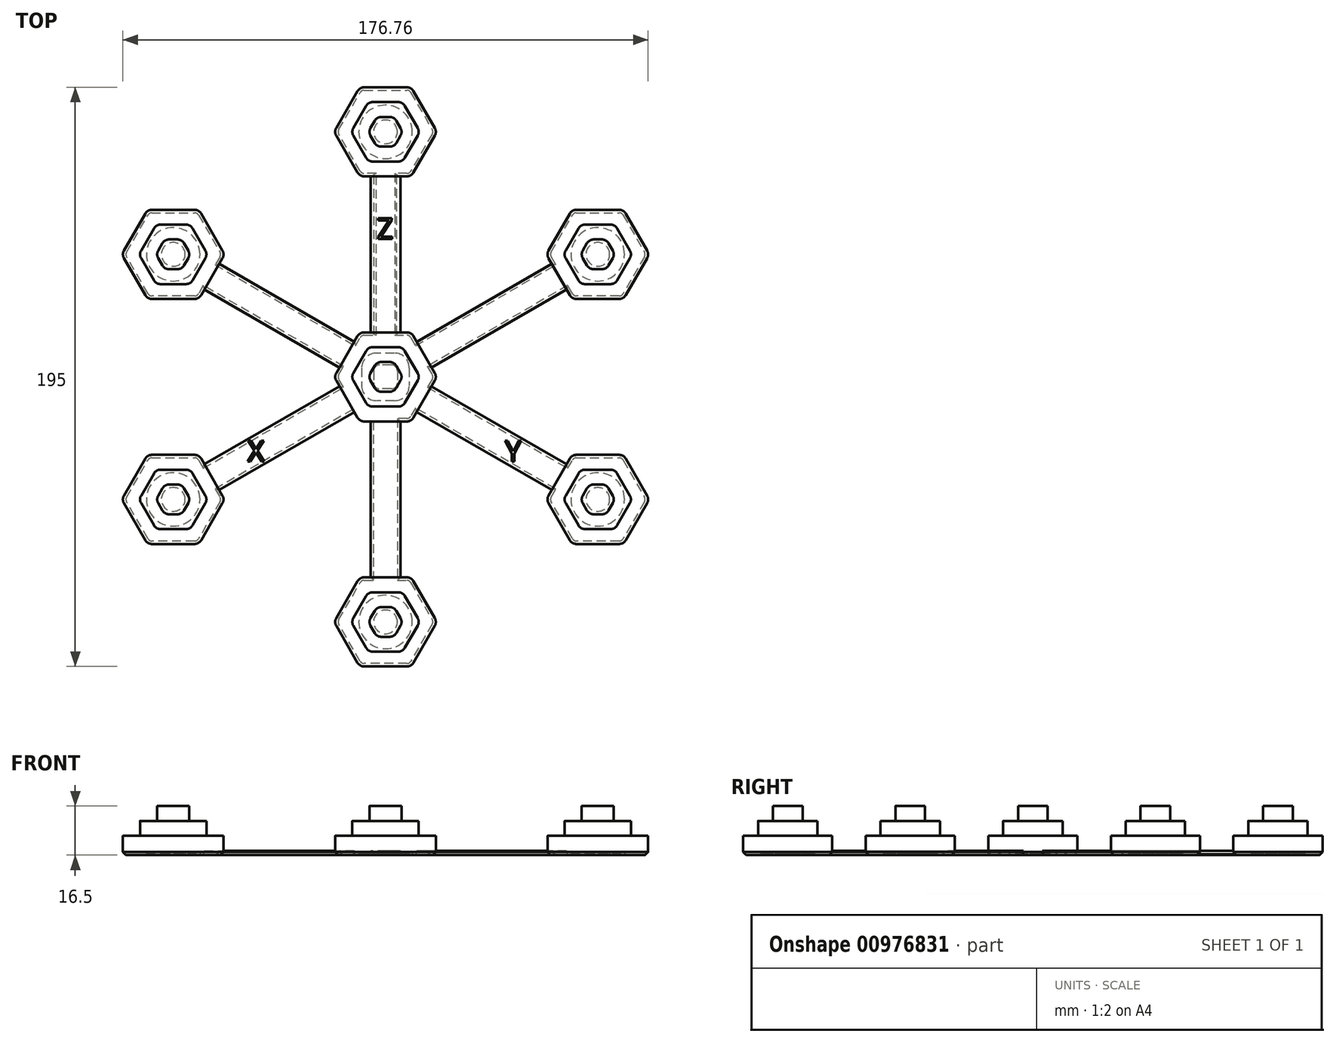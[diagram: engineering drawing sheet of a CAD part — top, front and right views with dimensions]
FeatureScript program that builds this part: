
annotation { "Feature Type Name" : "Feature", "Feature Type Description" : "" }
export const myFeature = defineFeature(function(context is Context, id is Id, definition is map)
    precondition{}
    {
        {
            var Q0;
            Q0=qCreatedBy(makeId("Top.planeOp"),FACE);
            var sketch = newSketch(context, id + "F0", { "sketchPlane" : qUnion([Q0])});
            skCircle(sketch, "E0", {"center": v(0, 0) * mm, "radius": 100 * mm, "construction": true});
            skCircle(sketch, "E1", {"center": v(0, 0) * mm, "radius": 65 * mm, "construction": true});
            skLineSegment(sketch, "E2", {"start": v(0, 0) * mm, "end": v(0, 82.5) * mm, "construction": true});
            skArc(sketch, "E3", {"start": v(5, 68.36) * mm, "mid": v(0, 97.5) * mm, "end": v(-5, 68.36) * mm, "construction": true});
            skLineSegment(sketch, "E4.1.0", {"start": v(0, 0) * mm, "end": v(-71.45, 41.25) * mm, "construction": true});
            skArc(sketch, "E4.1.1", {"start": v(-56.7, 38.5) * mm, "mid": v(-84.44, 48.75) * mm, "end": v(-61.7, 29.85) * mm, "construction": true});
            skLineSegment(sketch, "E4.2.0", {"start": v(0, 0) * mm, "end": v(-71.45, -41.25) * mm, "construction": true});
            skArc(sketch, "E4.2.1", {"start": v(-61.7, -29.85) * mm, "mid": v(-84.44, -48.75) * mm, "end": v(-56.7, -38.5) * mm, "construction": true});
            skLineSegment(sketch, "E4.3.0", {"start": v(0, 0) * mm, "end": v(0, -82.5) * mm, "construction": true});
            skArc(sketch, "E4.3.1", {"start": v(-5, -68.36) * mm, "mid": v(0, -97.5) * mm, "end": v(5, -68.36) * mm, "construction": true});
            skLineSegment(sketch, "E4.4.0", {"start": v(0, 0) * mm, "end": v(71.45, -41.25) * mm, "construction": true});
            skArc(sketch, "E4.4.1", {"start": v(56.7, -38.5) * mm, "mid": v(84.44, -48.75) * mm, "end": v(61.7, -29.85) * mm, "construction": true});
            skLineSegment(sketch, "E4.5.0", {"start": v(0, 0) * mm, "end": v(71.45, 41.25) * mm, "construction": true});
            skArc(sketch, "E4.5.1", {"start": v(61.7, 29.85) * mm, "mid": v(84.44, 48.75) * mm, "end": v(56.7, 38.5) * mm, "construction": true});
            skLineSegment(sketch, "E5.left", {"start": v(-5, 67.5) * mm, "end": v(-5, 15) * mm});
            skLineSegment(sketch, "E5.right", {"start": v(5, 67.5) * mm, "end": v(5, 15) * mm});
            skArc(sketch, "E6.trimOffspring", {"start": v(5, -14.14) * mm, "mid": v(7.5, -13) * mm, "end": v(9.75, -11.4) * mm});
            skCircle(sketch, "E7.cCircle", {"center": v(0, 82.5) * mm, "radius": 15 * mm, "construction": true});
            skLineSegment(sketch, "E7.0", {"start": v(-8.66, 97.5) * mm, "end": v(8.66, 97.5) * mm});
            skLineSegment(sketch, "E7.1", {"start": v(8.66, 97.5) * mm, "end": v(17.32, 82.5) * mm});
            skLineSegment(sketch, "E7.2", {"start": v(17.32, 82.5) * mm, "end": v(8.66, 67.5) * mm});
            skLineSegment(sketch, "E7.3", {"start": v(8.66, 67.5) * mm, "end": v(5, 67.5) * mm});
            skLineSegment(sketch, "E7.4", {"start": v(-8.66, 67.5) * mm, "end": v(-17.32, 82.5) * mm});
            skLineSegment(sketch, "E7.5", {"start": v(-17.32, 82.5) * mm, "end": v(-8.66, 97.5) * mm});
            skPoint(sketch, "E7.0.midPoint", {"position": v(0, 97.5) * mm});
            skLineSegment(sketch, "E8.trimOffspring", {"start": v(-5, 67.5) * mm, "end": v(-8.66, 67.5) * mm});
            skLineSegment(sketch, "E9.1.0", {"start": v(-80.1, 26.25) * mm, "end": v(-88.77, 41.25) * mm});
            skLineSegment(sketch, "E9.1.1", {"start": v(-88.77, 41.25) * mm, "end": v(-80.1, 56.25) * mm});
            skLineSegment(sketch, "E9.1.2", {"start": v(-80.1, 56.25) * mm, "end": v(-62.79, 56.25) * mm});
            skLineSegment(sketch, "E9.1.3", {"start": v(-62.79, 56.25) * mm, "end": v(-54.13, 41.25) * mm});
            skLineSegment(sketch, "E9.1.4", {"start": v(-62.79, 26.25) * mm, "end": v(-80.1, 26.25) * mm});
            skLineSegment(sketch, "E9.1.5", {"start": v(-60.96, 29.42) * mm, "end": v(-62.79, 26.25) * mm});
            skLineSegment(sketch, "E9.1.6", {"start": v(-54.13, 41.25) * mm, "end": v(-55.96, 38.08) * mm});
            skLineSegment(sketch, "E9.1.7", {"start": v(-60.96, 29.42) * mm, "end": v(-15.5, 3.17) * mm});
            skLineSegment(sketch, "E9.1.8", {"start": v(-55.96, 38.08) * mm, "end": v(-10.5, 11.83) * mm});
            skLineSegment(sketch, "E9.2.0", {"start": v(-62.79, -56.25) * mm, "end": v(-80.1, -56.25) * mm});
            skLineSegment(sketch, "E9.2.1", {"start": v(-80.1, -56.25) * mm, "end": v(-88.77, -41.25) * mm});
            skLineSegment(sketch, "E9.2.2", {"start": v(-88.77, -41.25) * mm, "end": v(-80.1, -26.25) * mm});
            skLineSegment(sketch, "E9.2.3", {"start": v(-80.1, -26.25) * mm, "end": v(-62.79, -26.25) * mm});
            skLineSegment(sketch, "E9.2.4", {"start": v(-54.13, -41.25) * mm, "end": v(-62.79, -56.25) * mm});
            skLineSegment(sketch, "E9.2.5", {"start": v(-55.96, -38.08) * mm, "end": v(-54.13, -41.25) * mm});
            skLineSegment(sketch, "E9.2.6", {"start": v(-62.79, -26.25) * mm, "end": v(-60.96, -29.42) * mm});
            skLineSegment(sketch, "E9.2.7", {"start": v(-55.96, -38.08) * mm, "end": v(-10.5, -11.83) * mm});
            skLineSegment(sketch, "E9.2.8", {"start": v(-60.96, -29.42) * mm, "end": v(-15.5, -3.17) * mm});
            skLineSegment(sketch, "E9.3.0", {"start": v(17.32, -82.5) * mm, "end": v(8.66, -97.5) * mm});
            skLineSegment(sketch, "E9.3.1", {"start": v(8.66, -97.5) * mm, "end": v(-8.66, -97.5) * mm});
            skLineSegment(sketch, "E9.3.2", {"start": v(-8.66, -97.5) * mm, "end": v(-17.32, -82.5) * mm});
            skLineSegment(sketch, "E9.3.3", {"start": v(-17.32, -82.5) * mm, "end": v(-8.66, -67.5) * mm});
            skLineSegment(sketch, "E9.3.4", {"start": v(8.66, -67.5) * mm, "end": v(17.32, -82.5) * mm});
            skLineSegment(sketch, "E9.3.5", {"start": v(5, -67.5) * mm, "end": v(8.66, -67.5) * mm});
            skLineSegment(sketch, "E9.3.6", {"start": v(-8.66, -67.5) * mm, "end": v(-5, -67.5) * mm});
            skLineSegment(sketch, "E9.3.7", {"start": v(5, -67.5) * mm, "end": v(5, -15) * mm});
            skLineSegment(sketch, "E9.3.8", {"start": v(-5, -67.5) * mm, "end": v(-5, -15) * mm});
            skLineSegment(sketch, "E9.4.0", {"start": v(80.1, -26.25) * mm, "end": v(88.77, -41.25) * mm});
            skLineSegment(sketch, "E9.4.1", {"start": v(88.77, -41.25) * mm, "end": v(80.1, -56.25) * mm});
            skLineSegment(sketch, "E9.4.2", {"start": v(80.1, -56.25) * mm, "end": v(62.79, -56.25) * mm});
            skLineSegment(sketch, "E9.4.3", {"start": v(62.79, -56.25) * mm, "end": v(54.13, -41.25) * mm});
            skLineSegment(sketch, "E9.4.4", {"start": v(62.79, -26.25) * mm, "end": v(80.1, -26.25) * mm});
            skLineSegment(sketch, "E9.4.5", {"start": v(60.96, -29.42) * mm, "end": v(62.79, -26.25) * mm});
            skLineSegment(sketch, "E9.4.6", {"start": v(54.13, -41.25) * mm, "end": v(55.96, -38.08) * mm});
            skLineSegment(sketch, "E9.4.7", {"start": v(60.96, -29.42) * mm, "end": v(15.5, -3.17) * mm});
            skLineSegment(sketch, "E9.4.8", {"start": v(55.96, -38.08) * mm, "end": v(10.5, -11.83) * mm});
            skLineSegment(sketch, "E9.5.0", {"start": v(62.79, 56.25) * mm, "end": v(80.1, 56.25) * mm});
            skLineSegment(sketch, "E9.5.1", {"start": v(80.1, 56.25) * mm, "end": v(88.77, 41.25) * mm});
            skLineSegment(sketch, "E9.5.2", {"start": v(88.77, 41.25) * mm, "end": v(80.1, 26.25) * mm});
            skLineSegment(sketch, "E9.5.3", {"start": v(80.1, 26.25) * mm, "end": v(62.79, 26.25) * mm});
            skLineSegment(sketch, "E9.5.4", {"start": v(54.13, 41.25) * mm, "end": v(62.79, 56.25) * mm});
            skLineSegment(sketch, "E9.5.5", {"start": v(55.96, 38.08) * mm, "end": v(54.13, 41.25) * mm});
            skLineSegment(sketch, "E9.5.6", {"start": v(62.79, 26.25) * mm, "end": v(60.96, 29.42) * mm});
            skLineSegment(sketch, "E9.5.7", {"start": v(55.96, 38.08) * mm, "end": v(10.5, 11.83) * mm});
            skLineSegment(sketch, "E9.5.8", {"start": v(60.96, 29.42) * mm, "end": v(15.5, 3.17) * mm});
            skCircle(sketch, "E10.cCircle", {"center": v(0, 0) * mm, "radius": 15 * mm, "construction": true});
            skLineSegment(sketch, "E10.0", {"start": v(8.66, -15) * mm, "end": v(5, -15) * mm});
            skLineSegment(sketch, "E10.1", {"start": v(-8.66, -15) * mm, "end": v(-10.5, -11.83) * mm});
            skLineSegment(sketch, "E10.2", {"start": v(-17.32, 0) * mm, "end": v(-15.5, 3.17) * mm});
            skLineSegment(sketch, "E10.3", {"start": v(-8.66, 15) * mm, "end": v(-5, 15) * mm});
            skLineSegment(sketch, "E10.4", {"start": v(8.66, 15) * mm, "end": v(10.5, 11.83) * mm});
            skLineSegment(sketch, "E10.5", {"start": v(17.32, 0) * mm, "end": v(15.5, -3.17) * mm});
            skPoint(sketch, "E10.0.midPoint", {"position": v(0, -15) * mm});
            skLineSegment(sketch, "E11.trimOffspring", {"start": v(5, 15) * mm, "end": v(8.66, 15) * mm});
            skPoint(sketch, "E12.orphan", {"position": v(5, 14.14) * mm});
            skPoint(sketch, "E13.orphan", {"position": v(-5, 14.14) * mm});
            skPoint(sketch, "E14.orphan", {"position": v(-9.75, 11.4) * mm});
            skLineSegment(sketch, "E15.trimOffspring", {"start": v(-10.5, 11.83) * mm, "end": v(-8.66, 15) * mm});
            skPoint(sketch, "E16.orphan", {"position": v(-14.75, 2.74) * mm});
            skLineSegment(sketch, "E17.trimOffspring", {"start": v(-15.5, -3.17) * mm, "end": v(-17.32, 0) * mm});
            skPoint(sketch, "E18.orphan", {"position": v(-14.75, -2.74) * mm});
            skPoint(sketch, "E19.orphan", {"position": v(-9.75, -11.4) * mm});
            skPoint(sketch, "E20.orphan", {"position": v(-5, -14.14) * mm});
            skLineSegment(sketch, "E21.trimOffspring", {"start": v(-5, -15) * mm, "end": v(-8.66, -15) * mm});
            skPoint(sketch, "E22.orphan", {"position": v(5, -14.14) * mm});
            skPoint(sketch, "E23.orphan", {"position": v(9.75, -11.4) * mm});
            skLineSegment(sketch, "E24.trimOffspring", {"start": v(10.5, -11.83) * mm, "end": v(8.66, -15) * mm});
            skPoint(sketch, "E25.orphan", {"position": v(14.75, -2.74) * mm});
            skPoint(sketch, "E26.orphan", {"position": v(9.75, 11.4) * mm});
            skLineSegment(sketch, "E27.trimOffspring", {"start": v(15.5, 3.17) * mm, "end": v(17.32, 0) * mm});
            skPoint(sketch, "E28.orphan", {"position": v(14.75, 2.74) * mm});
            skSolve(sketch);
        }
        {
            var Q0;
            Q0 = qSketchRegion(id + "F0", true);
            extrude(context, id + "F1", {"entities" : qUnion([Q0]), "depth" : 1.5 * mm, "offsetDistance" : 25 * mm});
        }
        {
            var Q0;
            Q0=makeQuery(id+"F1.opExtrude","CAP_FACE",FACE,{"disambiguationData":[OSD([sQuery(id+"F0.wireOp",EDGE,"E3"),sQuery(id+"F0.wireOp",EDGE,"E4.1.1"),sQuery(id+"F0.wireOp",EDGE,"E4.2.1"),sQuery(id+"F0.wireOp",EDGE,"E4.3.1"),sQuery(id+"F0.wireOp",EDGE,"E4.4.1"),sQuery(id+"F0.wireOp",EDGE,"E4.5.1"),sQuery(id+"F0.wireOp",EDGE,"d2wCPqSr-nOOy-JmX4-d6uT-xf62uPJMTqVu"),sQuery(id+"F0.wireOp",EDGE,"E5.left"),sQuery(id+"F0.wireOp",EDGE,"E5.right"),sQuery(id+"F0.wireOp",EDGE,"a48290ef-ed8c-49ca-b5e9-a96a2eef4f7f.1.0"),sQuery(id+"F0.wireOp",EDGE,"a48290ef-ed8c-49ca-b5e9-a96a2eef4f7f.1.2"),sQuery(id+"F0.wireOp",EDGE,"a48290ef-ed8c-49ca-b5e9-a96a2eef4f7f.2.0"),sQuery(id+"F0.wireOp",EDGE,"a48290ef-ed8c-49ca-b5e9-a96a2eef4f7f.2.2"),sQuery(id+"F0.wireOp",EDGE,"a48290ef-ed8c-49ca-b5e9-a96a2eef4f7f.3.0"),sQuery(id+"F0.wireOp",EDGE,"a48290ef-ed8c-49ca-b5e9-a96a2eef4f7f.3.2"),sQuery(id+"F0.wireOp",EDGE,"a48290ef-ed8c-49ca-b5e9-a96a2eef4f7f.4.0"),sQuery(id+"F0.wireOp",EDGE,"a48290ef-ed8c-49ca-b5e9-a96a2eef4f7f.4.2"),sQuery(id+"F0.wireOp",EDGE,"a48290ef-ed8c-49ca-b5e9-a96a2eef4f7f.5.0"),sQuery(id+"F0.wireOp",EDGE,"a48290ef-ed8c-49ca-b5e9-a96a2eef4f7f.5.2"),sQuery(id+"F0.wireOp",EDGE,"11eb75db-823b-41be-87a0-59ebbf35d80a.trimOffspring"),sQuery(id+"F0.wireOp",EDGE,"628562bd-411f-4c63-a98e-b396f9ac0886.trimOffspring"),sQuery(id+"F0.wireOp",EDGE,"E6.trimOffspring"),sQuery(id+"F0.wireOp",EDGE,"74142023-9392-48eb-a980-45bce0a610e0.trimOffspring"),sQuery(id+"F0.wireOp",EDGE,"74d19543-ae01-4b5b-b9fc-349c831204e3.trimOffspring")])],"isStart":false});
            var sketch = newSketch(context, id + "F2", { "sketchPlane" : qUnion([Q0])});
            skCircle(sketch, "E29.cCircle", {"center": v(0, 0) * mm, "radius": 15 * mm, "construction": true});
            skLineSegment(sketch, "E29.0", {"start": v(-8.66, 15) * mm, "end": v(8.66, 15) * mm});
            skLineSegment(sketch, "E29.1", {"start": v(8.66, 15) * mm, "end": v(17.32, 0) * mm});
            skLineSegment(sketch, "E29.2", {"start": v(17.32, 0) * mm, "end": v(8.66, -15) * mm});
            skLineSegment(sketch, "E29.3", {"start": v(8.66, -15) * mm, "end": v(-8.66, -15) * mm});
            skLineSegment(sketch, "E29.4", {"start": v(-8.66, -15) * mm, "end": v(-17.32, 0) * mm});
            skLineSegment(sketch, "E29.5", {"start": v(-17.32, 0) * mm, "end": v(-8.66, 15) * mm});
            skPoint(sketch, "E29.0.midPoint", {"position": v(0, 15) * mm});
            skCircle(sketch, "E30.cCircle", {"center": v(0, 82.5) * mm, "radius": 15 * mm, "construction": true});
            skLineSegment(sketch, "E30.0", {"start": v(-8.66, 97.5) * mm, "end": v(8.66, 97.5) * mm});
            skLineSegment(sketch, "E30.1", {"start": v(8.66, 97.5) * mm, "end": v(17.32, 82.5) * mm});
            skLineSegment(sketch, "E30.2", {"start": v(17.32, 82.5) * mm, "end": v(8.66, 67.5) * mm});
            skLineSegment(sketch, "E30.3", {"start": v(8.66, 67.5) * mm, "end": v(-8.66, 67.5) * mm});
            skLineSegment(sketch, "E30.4", {"start": v(-8.66, 67.5) * mm, "end": v(-17.32, 82.5) * mm});
            skLineSegment(sketch, "E30.5", {"start": v(-17.32, 82.5) * mm, "end": v(-8.66, 97.5) * mm});
            skPoint(sketch, "E30.0.midPoint", {"position": v(0, 97.5) * mm});
            skLineSegment(sketch, "E31.1.0", {"start": v(-80.1, 56.25) * mm, "end": v(-62.79, 56.25) * mm});
            skPoint(sketch, "E31.1.1", {"position": v(-84.44, 48.75) * mm});
            skLineSegment(sketch, "E31.1.2", {"start": v(-62.79, 56.25) * mm, "end": v(-54.13, 41.25) * mm});
            skLineSegment(sketch, "E31.1.3", {"start": v(-80.1, 26.25) * mm, "end": v(-88.77, 41.25) * mm});
            skCircle(sketch, "E31.1.4", {"center": v(-71.45, 41.25) * mm, "radius": 15 * mm, "construction": true});
            skLineSegment(sketch, "E31.1.5", {"start": v(-62.79, 26.25) * mm, "end": v(-80.1, 26.25) * mm});
            skLineSegment(sketch, "E31.1.6", {"start": v(-54.13, 41.25) * mm, "end": v(-62.79, 26.25) * mm});
            skLineSegment(sketch, "E31.1.7", {"start": v(-88.77, 41.25) * mm, "end": v(-80.1, 56.25) * mm});
            skLineSegment(sketch, "E31.2.0", {"start": v(-88.77, -41.25) * mm, "end": v(-80.1, -26.25) * mm});
            skPoint(sketch, "E31.2.1", {"position": v(-84.44, -48.75) * mm});
            skLineSegment(sketch, "E31.2.2", {"start": v(-80.1, -26.25) * mm, "end": v(-62.79, -26.25) * mm});
            skLineSegment(sketch, "E31.2.3", {"start": v(-62.79, -56.25) * mm, "end": v(-80.1, -56.25) * mm});
            skCircle(sketch, "E31.2.4", {"center": v(-71.45, -41.25) * mm, "radius": 15 * mm, "construction": true});
            skLineSegment(sketch, "E31.2.5", {"start": v(-54.13, -41.25) * mm, "end": v(-62.79, -56.25) * mm});
            skLineSegment(sketch, "E31.2.6", {"start": v(-62.79, -26.25) * mm, "end": v(-54.13, -41.25) * mm});
            skLineSegment(sketch, "E31.2.7", {"start": v(-80.1, -56.25) * mm, "end": v(-88.77, -41.25) * mm});
            skLineSegment(sketch, "E31.3.0", {"start": v(-8.66, -97.5) * mm, "end": v(-17.32, -82.5) * mm});
            skPoint(sketch, "E31.3.1", {"position": v(0, -97.5) * mm});
            skLineSegment(sketch, "E31.3.2", {"start": v(-17.32, -82.5) * mm, "end": v(-8.66, -67.5) * mm});
            skLineSegment(sketch, "E31.3.3", {"start": v(17.32, -82.5) * mm, "end": v(8.66, -97.5) * mm});
            skCircle(sketch, "E31.3.4", {"center": v(0, -82.5) * mm, "radius": 15 * mm, "construction": true});
            skLineSegment(sketch, "E31.3.5", {"start": v(8.66, -67.5) * mm, "end": v(17.32, -82.5) * mm});
            skLineSegment(sketch, "E31.3.6", {"start": v(-8.66, -67.5) * mm, "end": v(8.66, -67.5) * mm});
            skLineSegment(sketch, "E31.3.7", {"start": v(8.66, -97.5) * mm, "end": v(-8.66, -97.5) * mm});
            skLineSegment(sketch, "E31.4.0", {"start": v(80.1, -56.25) * mm, "end": v(62.79, -56.25) * mm});
            skPoint(sketch, "E31.4.1", {"position": v(84.44, -48.75) * mm});
            skLineSegment(sketch, "E31.4.2", {"start": v(62.79, -56.25) * mm, "end": v(54.13, -41.25) * mm});
            skLineSegment(sketch, "E31.4.3", {"start": v(80.1, -26.25) * mm, "end": v(88.77, -41.25) * mm});
            skCircle(sketch, "E31.4.4", {"center": v(71.45, -41.25) * mm, "radius": 15 * mm, "construction": true});
            skLineSegment(sketch, "E31.4.5", {"start": v(62.79, -26.25) * mm, "end": v(80.1, -26.25) * mm});
            skLineSegment(sketch, "E31.4.6", {"start": v(54.13, -41.25) * mm, "end": v(62.79, -26.25) * mm});
            skLineSegment(sketch, "E31.4.7", {"start": v(88.77, -41.25) * mm, "end": v(80.1, -56.25) * mm});
            skLineSegment(sketch, "E31.5.0", {"start": v(88.77, 41.25) * mm, "end": v(80.1, 26.25) * mm});
            skPoint(sketch, "E31.5.1", {"position": v(84.44, 48.75) * mm});
            skLineSegment(sketch, "E31.5.2", {"start": v(80.1, 26.25) * mm, "end": v(62.79, 26.25) * mm});
            skLineSegment(sketch, "E31.5.3", {"start": v(62.79, 56.25) * mm, "end": v(80.1, 56.25) * mm});
            skCircle(sketch, "E31.5.4", {"center": v(71.45, 41.25) * mm, "radius": 15 * mm, "construction": true});
            skLineSegment(sketch, "E31.5.5", {"start": v(54.13, 41.25) * mm, "end": v(62.79, 56.25) * mm});
            skLineSegment(sketch, "E31.5.6", {"start": v(62.79, 26.25) * mm, "end": v(54.13, 41.25) * mm});
            skLineSegment(sketch, "E31.5.7", {"start": v(80.1, 56.25) * mm, "end": v(88.77, 41.25) * mm});
            skSolve(sketch);
        }
        {
            var Q0;
            Q0 = qSketchRegion(id + "F2", true);
            extrude(context, id + "F3", {"entities" : qUnion([Q0]), "operationType" : NewBodyOperationType.ADD, "depth" : 5 * mm, "offsetDistance" : 25 * mm});
        }
        {
            var Q0;
            Q0=makeQuery(id+"F1.opExtrude","CAP_EDGE",EDGE,{"disambiguationData":[OSD([sQuery(id+"F0.wireOp",EDGE,"74142023-9392-48eb-a980-45bce0a610e0.trimOffspring")])],"isStart":true});
            var Q1;
            Q1=makeQuery(id+"F1.opExtrude","CAP_EDGE",EDGE,{"disambiguationData":[OSD([sQuery(id+"F0.wireOp",EDGE,"a48290ef-ed8c-49ca-b5e9-a96a2eef4f7f.3.2")])],"isStart":true});
            var Q2;
            Q2=makeQuery(id+"F1.opExtrude","CAP_EDGE",EDGE,{"disambiguationData":[OSD([sQuery(id+"F0.wireOp",EDGE,"E4.3.1")])],"isStart":true});
            var Q3;
            Q3=makeQuery(id+"F1.opExtrude","CAP_EDGE",EDGE,{"disambiguationData":[OSD([sQuery(id+"F0.wireOp",EDGE,"a48290ef-ed8c-49ca-b5e9-a96a2eef4f7f.3.0")])],"isStart":true});
            var Q4;
            Q4=makeQuery(id+"F1.opExtrude","CAP_EDGE",EDGE,{"disambiguationData":[OSD([sQuery(id+"F0.wireOp",EDGE,"E6.trimOffspring")])],"isStart":true});
            var Q5;
            Q5=makeQuery(id+"F1.opExtrude","CAP_EDGE",EDGE,{"disambiguationData":[OSD([sQuery(id+"F0.wireOp",EDGE,"a48290ef-ed8c-49ca-b5e9-a96a2eef4f7f.4.2")])],"isStart":true});
            var Q6;
            Q6=makeQuery(id+"F1.opExtrude","CAP_EDGE",EDGE,{"disambiguationData":[OSD([sQuery(id+"F0.wireOp",EDGE,"E4.4.1")])],"isStart":true});
            var Q7;
            Q7=makeQuery(id+"F1.opExtrude","CAP_EDGE",EDGE,{"disambiguationData":[OSD([sQuery(id+"F0.wireOp",EDGE,"a48290ef-ed8c-49ca-b5e9-a96a2eef4f7f.4.0")])],"isStart":true});
            var Q8;
            Q8=makeQuery(id+"F1.opExtrude","CAP_EDGE",EDGE,{"disambiguationData":[OSD([sQuery(id+"F0.wireOp",EDGE,"628562bd-411f-4c63-a98e-b396f9ac0886.trimOffspring")])],"isStart":true});
            var Q9;
            Q9=makeQuery(id+"F1.opExtrude","CAP_EDGE",EDGE,{"disambiguationData":[OSD([sQuery(id+"F0.wireOp",EDGE,"a48290ef-ed8c-49ca-b5e9-a96a2eef4f7f.5.2")])],"isStart":true});
            var Q10;
            Q10=makeQuery(id+"F1.opExtrude","CAP_EDGE",EDGE,{"disambiguationData":[OSD([sQuery(id+"F0.wireOp",EDGE,"E4.5.1")])],"isStart":true});
            var Q11;
            Q11=makeQuery(id+"F1.opExtrude","CAP_EDGE",EDGE,{"disambiguationData":[OSD([sQuery(id+"F0.wireOp",EDGE,"a48290ef-ed8c-49ca-b5e9-a96a2eef4f7f.5.0")])],"isStart":true});
            var Q12;
            Q12=makeQuery(id+"F1.opExtrude","CAP_EDGE",EDGE,{"disambiguationData":[OSD([sQuery(id+"F0.wireOp",EDGE,"11eb75db-823b-41be-87a0-59ebbf35d80a.trimOffspring")])],"isStart":true});
            var Q13;
            Q13=makeQuery(id+"F1.opExtrude","CAP_EDGE",EDGE,{"disambiguationData":[OSD([sQuery(id+"F0.wireOp",EDGE,"E5.right")])],"isStart":true});
            var Q14;
            Q14=makeQuery(id+"F1.opExtrude","CAP_EDGE",EDGE,{"disambiguationData":[OSD([sQuery(id+"F0.wireOp",EDGE,"E3")])],"isStart":true});
            var Q15;
            Q15=makeQuery(id+"F1.opExtrude","CAP_EDGE",EDGE,{"disambiguationData":[OSD([sQuery(id+"F0.wireOp",EDGE,"E5.left")])],"isStart":true});
            var Q16;
            Q16=makeQuery(id+"F1.opExtrude","CAP_EDGE",EDGE,{"disambiguationData":[OSD([sQuery(id+"F0.wireOp",EDGE,"d2wCPqSr-nOOy-JmX4-d6uT-xf62uPJMTqVu")])],"isStart":true});
            var Q17;
            Q17=makeQuery(id+"F1.opExtrude","CAP_EDGE",EDGE,{"disambiguationData":[OSD([sQuery(id+"F0.wireOp",EDGE,"a48290ef-ed8c-49ca-b5e9-a96a2eef4f7f.1.2")])],"isStart":true});
            var Q18;
            Q18=makeQuery(id+"F1.opExtrude","CAP_EDGE",EDGE,{"disambiguationData":[OSD([sQuery(id+"F0.wireOp",EDGE,"E4.1.1")])],"isStart":true});
            var Q19;
            Q19=makeQuery(id+"F1.opExtrude","CAP_EDGE",EDGE,{"disambiguationData":[OSD([sQuery(id+"F0.wireOp",EDGE,"a48290ef-ed8c-49ca-b5e9-a96a2eef4f7f.1.0")])],"isStart":true});
            var Q20;
            Q20=makeQuery(id+"F1.opExtrude","CAP_EDGE",EDGE,{"disambiguationData":[OSD([sQuery(id+"F0.wireOp",EDGE,"a48290ef-ed8c-49ca-b5e9-a96a2eef4f7f.2.0")])],"isStart":true});
            var Q21;
            Q21=makeQuery(id+"F1.opExtrude","CAP_EDGE",EDGE,{"disambiguationData":[OSD([sQuery(id+"F0.wireOp",EDGE,"74d19543-ae01-4b5b-b9fc-349c831204e3.trimOffspring")])],"isStart":true});
            var Q22;
            Q22=makeQuery(id+"F1.opExtrude","CAP_EDGE",EDGE,{"disambiguationData":[OSD([sQuery(id+"F0.wireOp",EDGE,"a48290ef-ed8c-49ca-b5e9-a96a2eef4f7f.2.2")])],"isStart":true});
            var Q23;
            Q23=makeQuery(id+"F1.opExtrude","CAP_EDGE",EDGE,{"disambiguationData":[OSD([sQuery(id+"F0.wireOp",EDGE,"E4.2.1")])],"isStart":true});
            chamfer(context, id + "F4", {"entities" : qUnion([Q0, Q1, Q2, Q3, Q4, Q5, Q6, Q7, Q8, Q9, Q10, Q11, Q12, Q13, Q14, Q15, Q16, Q17, Q18, Q19, Q20, Q21, Q22, Q23]), "width" : 1.5 * mm, "tangentPropagation" : true});
        }
        {
            var Q0;
            Q0=makeQuery(id+"F3.opExtrude","CAP_FACE",FACE,{"disambiguationData":[OSD([sQuery(id+"F2.wireOp",EDGE,"E29.0"),sQuery(id+"F2.wireOp",EDGE,"E29.1"),sQuery(id+"F2.wireOp",EDGE,"E29.2"),sQuery(id+"F2.wireOp",EDGE,"E29.3"),sQuery(id+"F2.wireOp",EDGE,"E29.4"),sQuery(id+"F2.wireOp",EDGE,"E29.5")])],"isStart":false});
            var sketch = newSketch(context, id + "F5", { "sketchPlane" : qUnion([Q0])});
            skCircle(sketch, "E32.cCircle", {"center": v(0, 0) * mm, "radius": 10 * mm, "construction": true});
            skLineSegment(sketch, "E32.0", {"start": v(-5.77, 10) * mm, "end": v(5.77, 10) * mm});
            skLineSegment(sketch, "E32.1", {"start": v(5.77, 10) * mm, "end": v(11.55, 0) * mm});
            skLineSegment(sketch, "E32.2", {"start": v(11.55, 0) * mm, "end": v(5.77, -10) * mm});
            skLineSegment(sketch, "E32.3", {"start": v(5.77, -10) * mm, "end": v(-5.77, -10) * mm});
            skLineSegment(sketch, "E32.4", {"start": v(-5.77, -10) * mm, "end": v(-11.55, 0) * mm});
            skLineSegment(sketch, "E32.5", {"start": v(-11.55, 0) * mm, "end": v(-5.77, 10) * mm});
            skPoint(sketch, "E32.0.midPoint", {"position": v(0, 10) * mm});
            skCircle(sketch, "E33.cCircle", {"center": v(0, 82.5) * mm, "radius": 10 * mm, "construction": true});
            skLineSegment(sketch, "E33.0", {"start": v(-5.77, 92.5) * mm, "end": v(5.77, 92.5) * mm});
            skLineSegment(sketch, "E33.1", {"start": v(5.77, 92.5) * mm, "end": v(11.55, 82.5) * mm});
            skLineSegment(sketch, "E33.2", {"start": v(11.55, 82.5) * mm, "end": v(5.77, 72.5) * mm});
            skLineSegment(sketch, "E33.3", {"start": v(5.77, 72.5) * mm, "end": v(-5.77, 72.5) * mm});
            skLineSegment(sketch, "E33.4", {"start": v(-5.77, 72.5) * mm, "end": v(-11.55, 82.5) * mm});
            skLineSegment(sketch, "E33.5", {"start": v(-11.55, 82.5) * mm, "end": v(-5.77, 92.5) * mm});
            skPoint(sketch, "E33.0.midPoint", {"position": v(0, 92.5) * mm});
            skLineSegment(sketch, "E34.1.0", {"start": v(-65.67, 51.25) * mm, "end": v(-59.9, 41.25) * mm});
            skLineSegment(sketch, "E34.1.1", {"start": v(-77.22, 51.25) * mm, "end": v(-65.67, 51.25) * mm});
            skLineSegment(sketch, "E34.1.2", {"start": v(-59.9, 41.25) * mm, "end": v(-65.67, 31.25) * mm});
            skCircle(sketch, "E34.1.3", {"center": v(-71.45, 41.25) * mm, "radius": 10 * mm, "construction": true});
            skPoint(sketch, "E34.1.4", {"position": v(-80.1, 46.25) * mm});
            skLineSegment(sketch, "E34.1.5", {"start": v(-65.67, 31.25) * mm, "end": v(-77.22, 31.25) * mm});
            skLineSegment(sketch, "E34.1.6", {"start": v(-77.22, 31.25) * mm, "end": v(-83, 41.25) * mm});
            skLineSegment(sketch, "E34.1.7", {"start": v(-83, 41.25) * mm, "end": v(-77.22, 51.25) * mm});
            skLineSegment(sketch, "E34.2.0", {"start": v(-77.22, -31.25) * mm, "end": v(-65.67, -31.25) * mm});
            skLineSegment(sketch, "E34.2.1", {"start": v(-83, -41.25) * mm, "end": v(-77.22, -31.25) * mm});
            skLineSegment(sketch, "E34.2.2", {"start": v(-65.67, -31.25) * mm, "end": v(-59.9, -41.25) * mm});
            skCircle(sketch, "E34.2.3", {"center": v(-71.45, -41.25) * mm, "radius": 10 * mm, "construction": true});
            skPoint(sketch, "E34.2.4", {"position": v(-80.1, -46.25) * mm});
            skLineSegment(sketch, "E34.2.5", {"start": v(-59.9, -41.25) * mm, "end": v(-65.67, -51.25) * mm});
            skLineSegment(sketch, "E34.2.6", {"start": v(-65.67, -51.25) * mm, "end": v(-77.22, -51.25) * mm});
            skLineSegment(sketch, "E34.2.7", {"start": v(-77.22, -51.25) * mm, "end": v(-83, -41.25) * mm});
            skLineSegment(sketch, "E34.3.0", {"start": v(-11.55, -82.5) * mm, "end": v(-5.77, -72.5) * mm});
            skLineSegment(sketch, "E34.3.1", {"start": v(-5.77, -92.5) * mm, "end": v(-11.55, -82.5) * mm});
            skLineSegment(sketch, "E34.3.2", {"start": v(-5.77, -72.5) * mm, "end": v(5.77, -72.5) * mm});
            skCircle(sketch, "E34.3.3", {"center": v(0, -82.5) * mm, "radius": 10 * mm, "construction": true});
            skPoint(sketch, "E34.3.4", {"position": v(0, -92.5) * mm});
            skLineSegment(sketch, "E34.3.5", {"start": v(5.77, -72.5) * mm, "end": v(11.55, -82.5) * mm});
            skLineSegment(sketch, "E34.3.6", {"start": v(11.55, -82.5) * mm, "end": v(5.77, -92.5) * mm});
            skLineSegment(sketch, "E34.3.7", {"start": v(5.77, -92.5) * mm, "end": v(-5.77, -92.5) * mm});
            skLineSegment(sketch, "E34.4.0", {"start": v(65.67, -51.25) * mm, "end": v(59.9, -41.25) * mm});
            skLineSegment(sketch, "E34.4.1", {"start": v(77.22, -51.25) * mm, "end": v(65.67, -51.25) * mm});
            skLineSegment(sketch, "E34.4.2", {"start": v(59.9, -41.25) * mm, "end": v(65.67, -31.25) * mm});
            skCircle(sketch, "E34.4.3", {"center": v(71.45, -41.25) * mm, "radius": 10 * mm, "construction": true});
            skPoint(sketch, "E34.4.4", {"position": v(80.1, -46.25) * mm});
            skLineSegment(sketch, "E34.4.5", {"start": v(65.67, -31.25) * mm, "end": v(77.22, -31.25) * mm});
            skLineSegment(sketch, "E34.4.6", {"start": v(77.22, -31.25) * mm, "end": v(83, -41.25) * mm});
            skLineSegment(sketch, "E34.4.7", {"start": v(83, -41.25) * mm, "end": v(77.22, -51.25) * mm});
            skLineSegment(sketch, "E34.5.0", {"start": v(77.22, 31.25) * mm, "end": v(65.67, 31.25) * mm});
            skLineSegment(sketch, "E34.5.1", {"start": v(83, 41.25) * mm, "end": v(77.22, 31.25) * mm});
            skLineSegment(sketch, "E34.5.2", {"start": v(65.67, 31.25) * mm, "end": v(59.9, 41.25) * mm});
            skCircle(sketch, "E34.5.3", {"center": v(71.45, 41.25) * mm, "radius": 10 * mm, "construction": true});
            skPoint(sketch, "E34.5.4", {"position": v(80.1, 46.25) * mm});
            skLineSegment(sketch, "E34.5.5", {"start": v(59.9, 41.25) * mm, "end": v(65.67, 51.25) * mm});
            skLineSegment(sketch, "E34.5.6", {"start": v(65.67, 51.25) * mm, "end": v(77.22, 51.25) * mm});
            skLineSegment(sketch, "E34.5.7", {"start": v(77.22, 51.25) * mm, "end": v(83, 41.25) * mm});
            skSolve(sketch);
        }
        {
            var Q0;
            Q0 = qSketchRegion(id + "F5", true);
            extrude(context, id + "F6", {"entities" : qUnion([Q0]), "operationType" : NewBodyOperationType.ADD, "depth" : 5 * mm, "offsetDistance" : 25 * mm});
        }
        {
            var Q0;
            Q0=makeQuery(id+"F6.opExtrude","CAP_FACE",FACE,{"disambiguationData":[OSD([sQuery(id+"F5.wireOp",EDGE,"E32.0"),sQuery(id+"F5.wireOp",EDGE,"E32.1"),sQuery(id+"F5.wireOp",EDGE,"E32.2"),sQuery(id+"F5.wireOp",EDGE,"E32.3"),sQuery(id+"F5.wireOp",EDGE,"E32.4"),sQuery(id+"F5.wireOp",EDGE,"E32.5")])],"isStart":false});
            var sketch = newSketch(context, id + "F7", { "sketchPlane" : qUnion([Q0])});
            skCircle(sketch, "E35.cCircle", {"center": v(0, 0) * mm, "radius": 5 * mm, "construction": true});
            skLineSegment(sketch, "E35.0", {"start": v(-2.89, 5) * mm, "end": v(2.89, 5) * mm});
            skLineSegment(sketch, "E35.1", {"start": v(2.89, 5) * mm, "end": v(5.77, 0) * mm});
            skLineSegment(sketch, "E35.2", {"start": v(5.77, 0) * mm, "end": v(2.89, -5) * mm});
            skLineSegment(sketch, "E35.3", {"start": v(2.89, -5) * mm, "end": v(-2.89, -5) * mm});
            skLineSegment(sketch, "E35.4", {"start": v(-2.89, -5) * mm, "end": v(-5.77, 0) * mm});
            skLineSegment(sketch, "E35.5", {"start": v(-5.77, 0) * mm, "end": v(-2.89, 5) * mm});
            skPoint(sketch, "E35.0.midPoint", {"position": v(0, 5) * mm});
            skCircle(sketch, "E36.cCircle", {"center": v(0, 82.5) * mm, "radius": 5 * mm, "construction": true});
            skLineSegment(sketch, "E36.0", {"start": v(-2.89, 87.5) * mm, "end": v(2.89, 87.5) * mm});
            skLineSegment(sketch, "E36.1", {"start": v(2.89, 87.5) * mm, "end": v(5.77, 82.5) * mm});
            skLineSegment(sketch, "E36.2", {"start": v(5.77, 82.5) * mm, "end": v(2.89, 77.5) * mm});
            skLineSegment(sketch, "E36.3", {"start": v(2.89, 77.5) * mm, "end": v(-2.89, 77.5) * mm});
            skLineSegment(sketch, "E36.4", {"start": v(-2.89, 77.5) * mm, "end": v(-5.77, 82.5) * mm});
            skLineSegment(sketch, "E36.5", {"start": v(-5.77, 82.5) * mm, "end": v(-2.89, 87.5) * mm});
            skPoint(sketch, "E36.0.midPoint", {"position": v(0, 87.5) * mm});
            skPoint(sketch, "E37.1.0", {"position": v(-75.78, 43.75) * mm});
            skLineSegment(sketch, "E37.1.1", {"start": v(-74.33, 46.25) * mm, "end": v(-68.56, 46.25) * mm});
            skLineSegment(sketch, "E37.1.2", {"start": v(-68.56, 46.25) * mm, "end": v(-65.67, 41.25) * mm});
            skLineSegment(sketch, "E37.1.3", {"start": v(-65.67, 41.25) * mm, "end": v(-68.56, 36.25) * mm});
            skLineSegment(sketch, "E37.1.4", {"start": v(-74.33, 36.25) * mm, "end": v(-77.22, 41.25) * mm});
            skLineSegment(sketch, "E37.1.5", {"start": v(-77.22, 41.25) * mm, "end": v(-74.33, 46.25) * mm});
            skLineSegment(sketch, "E37.1.6", {"start": v(-68.56, 36.25) * mm, "end": v(-74.33, 36.25) * mm});
            skCircle(sketch, "E37.1.7", {"center": v(-71.45, 41.25) * mm, "radius": 5 * mm, "construction": true});
            skPoint(sketch, "E37.2.0", {"position": v(-75.78, -43.75) * mm});
            skLineSegment(sketch, "E37.2.1", {"start": v(-77.22, -41.25) * mm, "end": v(-74.33, -36.25) * mm});
            skLineSegment(sketch, "E37.2.2", {"start": v(-74.33, -36.25) * mm, "end": v(-68.56, -36.25) * mm});
            skLineSegment(sketch, "E37.2.3", {"start": v(-68.56, -36.25) * mm, "end": v(-65.67, -41.25) * mm});
            skLineSegment(sketch, "E37.2.4", {"start": v(-68.56, -46.25) * mm, "end": v(-74.33, -46.25) * mm});
            skLineSegment(sketch, "E37.2.5", {"start": v(-74.33, -46.25) * mm, "end": v(-77.22, -41.25) * mm});
            skLineSegment(sketch, "E37.2.6", {"start": v(-65.67, -41.25) * mm, "end": v(-68.56, -46.25) * mm});
            skCircle(sketch, "E37.2.7", {"center": v(-71.45, -41.25) * mm, "radius": 5 * mm, "construction": true});
            skPoint(sketch, "E37.3.0", {"position": v(0, -87.5) * mm});
            skLineSegment(sketch, "E37.3.1", {"start": v(-2.89, -87.5) * mm, "end": v(-5.77, -82.5) * mm});
            skLineSegment(sketch, "E37.3.2", {"start": v(-5.77, -82.5) * mm, "end": v(-2.89, -77.5) * mm});
            skLineSegment(sketch, "E37.3.3", {"start": v(-2.89, -77.5) * mm, "end": v(2.89, -77.5) * mm});
            skLineSegment(sketch, "E37.3.4", {"start": v(5.77, -82.5) * mm, "end": v(2.89, -87.5) * mm});
            skLineSegment(sketch, "E37.3.5", {"start": v(2.89, -87.5) * mm, "end": v(-2.89, -87.5) * mm});
            skLineSegment(sketch, "E37.3.6", {"start": v(2.89, -77.5) * mm, "end": v(5.77, -82.5) * mm});
            skCircle(sketch, "E37.3.7", {"center": v(0, -82.5) * mm, "radius": 5 * mm, "construction": true});
            skPoint(sketch, "E37.4.0", {"position": v(75.78, -43.75) * mm});
            skLineSegment(sketch, "E37.4.1", {"start": v(74.33, -46.25) * mm, "end": v(68.56, -46.25) * mm});
            skLineSegment(sketch, "E37.4.2", {"start": v(68.56, -46.25) * mm, "end": v(65.67, -41.25) * mm});
            skLineSegment(sketch, "E37.4.3", {"start": v(65.67, -41.25) * mm, "end": v(68.56, -36.25) * mm});
            skLineSegment(sketch, "E37.4.4", {"start": v(74.33, -36.25) * mm, "end": v(77.22, -41.25) * mm});
            skLineSegment(sketch, "E37.4.5", {"start": v(77.22, -41.25) * mm, "end": v(74.33, -46.25) * mm});
            skLineSegment(sketch, "E37.4.6", {"start": v(68.56, -36.25) * mm, "end": v(74.33, -36.25) * mm});
            skCircle(sketch, "E37.4.7", {"center": v(71.45, -41.25) * mm, "radius": 5 * mm, "construction": true});
            skPoint(sketch, "E37.5.0", {"position": v(75.78, 43.75) * mm});
            skLineSegment(sketch, "E37.5.1", {"start": v(77.22, 41.25) * mm, "end": v(74.33, 36.25) * mm});
            skLineSegment(sketch, "E37.5.2", {"start": v(74.33, 36.25) * mm, "end": v(68.56, 36.25) * mm});
            skLineSegment(sketch, "E37.5.3", {"start": v(68.56, 36.25) * mm, "end": v(65.67, 41.25) * mm});
            skLineSegment(sketch, "E37.5.4", {"start": v(68.56, 46.25) * mm, "end": v(74.33, 46.25) * mm});
            skLineSegment(sketch, "E37.5.5", {"start": v(74.33, 46.25) * mm, "end": v(77.22, 41.25) * mm});
            skLineSegment(sketch, "E37.5.6", {"start": v(65.67, 41.25) * mm, "end": v(68.56, 46.25) * mm});
            skCircle(sketch, "E37.5.7", {"center": v(71.45, 41.25) * mm, "radius": 5 * mm, "construction": true});
            skSolve(sketch);
        }
        {
            var Q0;
            Q0 = qSketchRegion(id + "F7", true);
            extrude(context, id + "F8", {"entities" : qUnion([Q0]), "operationType" : NewBodyOperationType.ADD, "depth" : 5 * mm, "offsetDistance" : 25 * mm});
        }
        {
            var Q0;
            Q0=makeQuery(id+"F1.opExtrude","CAP_FACE",FACE,{"disambiguationData":[OSD([sQuery(id+"F0.wireOp",EDGE,"E3"),sQuery(id+"F0.wireOp",EDGE,"E4.1.1"),sQuery(id+"F0.wireOp",EDGE,"E4.2.1"),sQuery(id+"F0.wireOp",EDGE,"E4.3.1"),sQuery(id+"F0.wireOp",EDGE,"E4.4.1"),sQuery(id+"F0.wireOp",EDGE,"E4.5.1"),sQuery(id+"F0.wireOp",EDGE,"d2wCPqSr-nOOy-JmX4-d6uT-xf62uPJMTqVu"),sQuery(id+"F0.wireOp",EDGE,"E5.left"),sQuery(id+"F0.wireOp",EDGE,"E5.right"),sQuery(id+"F0.wireOp",EDGE,"a48290ef-ed8c-49ca-b5e9-a96a2eef4f7f.1.0"),sQuery(id+"F0.wireOp",EDGE,"a48290ef-ed8c-49ca-b5e9-a96a2eef4f7f.1.2"),sQuery(id+"F0.wireOp",EDGE,"a48290ef-ed8c-49ca-b5e9-a96a2eef4f7f.2.0"),sQuery(id+"F0.wireOp",EDGE,"a48290ef-ed8c-49ca-b5e9-a96a2eef4f7f.2.2"),sQuery(id+"F0.wireOp",EDGE,"a48290ef-ed8c-49ca-b5e9-a96a2eef4f7f.3.0"),sQuery(id+"F0.wireOp",EDGE,"a48290ef-ed8c-49ca-b5e9-a96a2eef4f7f.3.2"),sQuery(id+"F0.wireOp",EDGE,"a48290ef-ed8c-49ca-b5e9-a96a2eef4f7f.4.0"),sQuery(id+"F0.wireOp",EDGE,"a48290ef-ed8c-49ca-b5e9-a96a2eef4f7f.4.2"),sQuery(id+"F0.wireOp",EDGE,"a48290ef-ed8c-49ca-b5e9-a96a2eef4f7f.5.0"),sQuery(id+"F0.wireOp",EDGE,"a48290ef-ed8c-49ca-b5e9-a96a2eef4f7f.5.2"),sQuery(id+"F0.wireOp",EDGE,"11eb75db-823b-41be-87a0-59ebbf35d80a.trimOffspring"),sQuery(id+"F0.wireOp",EDGE,"628562bd-411f-4c63-a98e-b396f9ac0886.trimOffspring"),sQuery(id+"F0.wireOp",EDGE,"E6.trimOffspring"),sQuery(id+"F0.wireOp",EDGE,"74142023-9392-48eb-a980-45bce0a610e0.trimOffspring"),sQuery(id+"F0.wireOp",EDGE,"74d19543-ae01-4b5b-b9fc-349c831204e3.trimOffspring")])],"isStart":true});
            var sketch = newSketch(context, id + "F9", { "sketchPlane" : qUnion([Q0])});
            skLineSegment(sketch, "E38.bottom", {"start": v(8, -8) * mm, "end": v(-8, -8) * mm});
            skLineSegment(sketch, "E38.top", {"start": v(8, 8) * mm, "end": v(-8, 8) * mm});
            skLineSegment(sketch, "E38.left", {"start": v(8, -8) * mm, "end": v(8, 8) * mm});
            skLineSegment(sketch, "E38.right", {"start": v(-8, -8) * mm, "end": v(-8, 8) * mm});
            skPoint(sketch, "E38.middle", {"position": v(0, 0) * mm});
            skLineSegment(sketch, "E39.bottom", {"start": v(4, -4) * mm, "end": v(-4, -4) * mm});
            skLineSegment(sketch, "E39.top", {"start": v(4, 4) * mm, "end": v(-4, 4) * mm});
            skLineSegment(sketch, "E39.left", {"start": v(4, -4) * mm, "end": v(4, 4) * mm});
            skLineSegment(sketch, "E39.right", {"start": v(-4, -4) * mm, "end": v(-4, 4) * mm});
            skSolve(sketch);
        }
        {
            var Q0;
            Q0 = qSketchRegion(id + "F9", true);
            extrude(context, id + "F10", {"entities" : qUnion([Q0]), "operationType" : NewBodyOperationType.REMOVE, "oppositeDirection" : true, "depth" : 0.5 * mm, "offsetDistance" : 25 * mm});
        }
        {
            var Q0;
            Q0=makeQuery(id+"F10.boolean.opBoolean","COPY",EDGE,{"derivedFrom":makeQuery(id+"F10.opExtrude","SWEPT_EDGE",EDGE,{"disambiguationData":[OSD([sQuery(id+"F9.wireOp",EDGE,"E38.top"),sQuery(id+"F9.wireOp",EDGE,"E38.right")])]})});
            var Q1;
            Q1=makeQuery(id+"F10.boolean.opBoolean","COPY",EDGE,{"derivedFrom":makeQuery(id+"F10.opExtrude","SWEPT_EDGE",EDGE,{"disambiguationData":[OSD([sQuery(id+"F9.wireOp",EDGE,"E38.top"),sQuery(id+"F9.wireOp",EDGE,"E38.left")])]})});
            var Q2;
            Q2=makeQuery(id+"F10.boolean.opBoolean","COPY",EDGE,{"derivedFrom":makeQuery(id+"F10.opExtrude","SWEPT_EDGE",EDGE,{"disambiguationData":[OSD([sQuery(id+"F9.wireOp",EDGE,"E38.bottom"),sQuery(id+"F9.wireOp",EDGE,"E38.left")])]})});
            var Q3;
            Q3=makeQuery(id+"F10.boolean.opBoolean","COPY",EDGE,{"derivedFrom":makeQuery(id+"F10.opExtrude","SWEPT_EDGE",EDGE,{"disambiguationData":[OSD([sQuery(id+"F9.wireOp",EDGE,"E38.bottom"),sQuery(id+"F9.wireOp",EDGE,"E38.right")])]})});
            fillet(context, id + "F11", {"entities" : qUnion([Q0, Q1, Q2, Q3]), "radius" : 5 * mm, "tangentPropagation" : true, "allowEdgeOverflow" : false});
        }
        {
            var Q0;
            Q0=makeQuery(id+"F10.boolean.opBoolean","COPY",EDGE,{"derivedFrom":makeQuery(id+"F10.opExtrude","SWEPT_EDGE",EDGE,{"disambiguationData":[OSD([sQuery(id+"F9.wireOp",EDGE,"E39.bottom"),sQuery(id+"F9.wireOp",EDGE,"E39.left")])]})});
            var Q1;
            Q1=makeQuery(id+"F10.boolean.opBoolean","COPY",EDGE,{"derivedFrom":makeQuery(id+"F10.opExtrude","SWEPT_EDGE",EDGE,{"disambiguationData":[OSD([sQuery(id+"F9.wireOp",EDGE,"E39.bottom"),sQuery(id+"F9.wireOp",EDGE,"E39.right")])]})});
            var Q2;
            Q2=makeQuery(id+"F10.boolean.opBoolean","COPY",EDGE,{"derivedFrom":makeQuery(id+"F10.opExtrude","SWEPT_EDGE",EDGE,{"disambiguationData":[OSD([sQuery(id+"F9.wireOp",EDGE,"E39.top"),sQuery(id+"F9.wireOp",EDGE,"E39.right")])]})});
            var Q3;
            Q3=makeQuery(id+"F10.boolean.opBoolean","COPY",EDGE,{"derivedFrom":makeQuery(id+"F10.opExtrude","SWEPT_EDGE",EDGE,{"disambiguationData":[OSD([sQuery(id+"F9.wireOp",EDGE,"E39.top"),sQuery(id+"F9.wireOp",EDGE,"E39.left")])]})});
            fillet(context, id + "F12", {"entities" : qUnion([Q0, Q1, Q2, Q3]), "radius" : 2 * mm, "tangentPropagation" : true, "allowEdgeOverflow" : false});
        }
        {
            var Q0;
            Q0=makeQuery(id+"F3.boolean.opBoolean","MERGE",EDGE,{"derivedFrom":[makeQuery(id+"F1.opExtrude","SWEPT_EDGE",EDGE,{"disambiguationData":[OSD([sQuery(id+"F0.wireOp",EDGE,"E9.3.1"),sQuery(id+"F0.wireOp",EDGE,"E9.3.2")])]}),makeQuery(id+"F3.opExtrude","SWEPT_EDGE",EDGE,{"disambiguationData":[OSD([sQuery(id+"F2.wireOp",EDGE,"E31.3.0"),sQuery(id+"F2.wireOp",EDGE,"E31.3.7")])]})]});
            var Q1;
            Q1=makeQuery(id+"F3.boolean.opBoolean","MERGE",EDGE,{"derivedFrom":[makeQuery(id+"F1.opExtrude","SWEPT_EDGE",EDGE,{"disambiguationData":[OSD([sQuery(id+"F0.wireOp",EDGE,"E9.3.0"),sQuery(id+"F0.wireOp",EDGE,"E9.3.1")])]}),makeQuery(id+"F3.opExtrude","SWEPT_EDGE",EDGE,{"disambiguationData":[OSD([sQuery(id+"F2.wireOp",EDGE,"E31.3.3"),sQuery(id+"F2.wireOp",EDGE,"E31.3.7")])]})]});
            var Q2;
            Q2=makeQuery(id+"F3.boolean.opBoolean","MERGE",EDGE,{"derivedFrom":[makeQuery(id+"F1.opExtrude","SWEPT_EDGE",EDGE,{"disambiguationData":[OSD([sQuery(id+"F0.wireOp",EDGE,"E9.3.0"),sQuery(id+"F0.wireOp",EDGE,"E9.3.4")])]}),makeQuery(id+"F3.opExtrude","SWEPT_EDGE",EDGE,{"disambiguationData":[OSD([sQuery(id+"F2.wireOp",EDGE,"E31.3.3"),sQuery(id+"F2.wireOp",EDGE,"E31.3.5")])]})]});
            var Q3;
            Q3=makeQuery(id+"F3.boolean.opBoolean","MERGE",EDGE,{"derivedFrom":[makeQuery(id+"F1.opExtrude","SWEPT_EDGE",EDGE,{"disambiguationData":[OSD([sQuery(id+"F0.wireOp",EDGE,"E9.3.4"),sQuery(id+"F0.wireOp",EDGE,"E9.3.5")])]}),makeQuery(id+"F3.opExtrude","SWEPT_EDGE",EDGE,{"disambiguationData":[OSD([sQuery(id+"F2.wireOp",EDGE,"E31.3.5"),sQuery(id+"F2.wireOp",EDGE,"E31.3.6")])]})]});
            var Q4;
            Q4=makeQuery(id+"F3.boolean.opBoolean","MERGE",EDGE,{"derivedFrom":[makeQuery(id+"F1.opExtrude","SWEPT_EDGE",EDGE,{"disambiguationData":[OSD([sQuery(id+"F0.wireOp",EDGE,"E9.3.3"),sQuery(id+"F0.wireOp",EDGE,"E9.3.6")])]}),makeQuery(id+"F3.opExtrude","SWEPT_EDGE",EDGE,{"disambiguationData":[OSD([sQuery(id+"F2.wireOp",EDGE,"E31.3.2"),sQuery(id+"F2.wireOp",EDGE,"E31.3.6")])]})]});
            var Q5;
            Q5=makeQuery(id+"F3.boolean.opBoolean","MERGE",EDGE,{"derivedFrom":[makeQuery(id+"F1.opExtrude","SWEPT_EDGE",EDGE,{"disambiguationData":[OSD([sQuery(id+"F0.wireOp",EDGE,"E9.3.2"),sQuery(id+"F0.wireOp",EDGE,"E9.3.3")])]}),makeQuery(id+"F3.opExtrude","SWEPT_EDGE",EDGE,{"disambiguationData":[OSD([sQuery(id+"F2.wireOp",EDGE,"E31.3.0"),sQuery(id+"F2.wireOp",EDGE,"E31.3.2")])]})]});
            var Q6;
            Q6=makeQuery(id+"F6.opExtrude","SWEPT_EDGE",EDGE,{"disambiguationData":[OSD([sQuery(id+"F5.wireOp",EDGE,"E34.3.1"),sQuery(id+"F5.wireOp",EDGE,"E34.3.7")])]});
            var Q7;
            Q7=makeQuery(id+"F6.opExtrude","SWEPT_EDGE",EDGE,{"disambiguationData":[OSD([sQuery(id+"F5.wireOp",EDGE,"E34.3.0"),sQuery(id+"F5.wireOp",EDGE,"E34.3.1")])]});
            var Q8;
            Q8=makeQuery(id+"F6.opExtrude","SWEPT_EDGE",EDGE,{"disambiguationData":[OSD([sQuery(id+"F5.wireOp",EDGE,"E34.3.0"),sQuery(id+"F5.wireOp",EDGE,"E34.3.2")])]});
            var Q9;
            Q9=makeQuery(id+"F6.opExtrude","SWEPT_EDGE",EDGE,{"disambiguationData":[OSD([sQuery(id+"F5.wireOp",EDGE,"E34.3.2"),sQuery(id+"F5.wireOp",EDGE,"E34.3.5")])]});
            var Q10;
            Q10=makeQuery(id+"F6.opExtrude","SWEPT_EDGE",EDGE,{"disambiguationData":[OSD([sQuery(id+"F5.wireOp",EDGE,"E34.3.5"),sQuery(id+"F5.wireOp",EDGE,"E34.3.6")])]});
            var Q11;
            Q11=makeQuery(id+"F6.opExtrude","SWEPT_EDGE",EDGE,{"disambiguationData":[OSD([sQuery(id+"F5.wireOp",EDGE,"E34.3.6"),sQuery(id+"F5.wireOp",EDGE,"E34.3.7")])]});
            var Q12;
            Q12=makeQuery(id+"F8.opExtrude","SWEPT_EDGE",EDGE,{"disambiguationData":[OSD([sQuery(id+"F7.wireOp",EDGE,"E37.3.4"),sQuery(id+"F7.wireOp",EDGE,"E37.3.5")])]});
            var Q13;
            Q13=makeQuery(id+"F8.opExtrude","SWEPT_EDGE",EDGE,{"disambiguationData":[OSD([sQuery(id+"F7.wireOp",EDGE,"E37.3.1"),sQuery(id+"F7.wireOp",EDGE,"E37.3.5")])]});
            var Q14;
            Q14=makeQuery(id+"F8.opExtrude","SWEPT_EDGE",EDGE,{"disambiguationData":[OSD([sQuery(id+"F7.wireOp",EDGE,"E37.3.1"),sQuery(id+"F7.wireOp",EDGE,"E37.3.2")])]});
            var Q15;
            Q15=makeQuery(id+"F8.opExtrude","SWEPT_EDGE",EDGE,{"disambiguationData":[OSD([sQuery(id+"F7.wireOp",EDGE,"E37.3.2"),sQuery(id+"F7.wireOp",EDGE,"E37.3.3")])]});
            var Q16;
            Q16=makeQuery(id+"F8.opExtrude","SWEPT_EDGE",EDGE,{"disambiguationData":[OSD([sQuery(id+"F7.wireOp",EDGE,"E37.3.4"),sQuery(id+"F7.wireOp",EDGE,"E37.3.6")])]});
            var Q17;
            Q17=makeQuery(id+"F8.opExtrude","SWEPT_EDGE",EDGE,{"disambiguationData":[OSD([sQuery(id+"F7.wireOp",EDGE,"E37.3.3"),sQuery(id+"F7.wireOp",EDGE,"E37.3.6")])]});
            var Q18;
            Q18=makeQuery(id+"F3.boolean.opBoolean","MERGE",EDGE,{"derivedFrom":[makeQuery(id+"F1.opExtrude","SWEPT_EDGE",EDGE,{"disambiguationData":[OSD([sQuery(id+"F0.wireOp",EDGE,"E9.2.0"),sQuery(id+"F0.wireOp",EDGE,"E9.2.4")])]}),makeQuery(id+"F3.opExtrude","SWEPT_EDGE",EDGE,{"disambiguationData":[OSD([sQuery(id+"F2.wireOp",EDGE,"E31.2.3"),sQuery(id+"F2.wireOp",EDGE,"E31.2.5")])]})]});
            var Q19;
            Q19=makeQuery(id+"F3.boolean.opBoolean","MERGE",EDGE,{"derivedFrom":[makeQuery(id+"F1.opExtrude","SWEPT_EDGE",EDGE,{"disambiguationData":[OSD([sQuery(id+"F0.wireOp",EDGE,"E9.2.0"),sQuery(id+"F0.wireOp",EDGE,"E9.2.1")])]}),makeQuery(id+"F3.opExtrude","SWEPT_EDGE",EDGE,{"disambiguationData":[OSD([sQuery(id+"F2.wireOp",EDGE,"E31.2.3"),sQuery(id+"F2.wireOp",EDGE,"E31.2.7")])]})]});
            var Q20;
            Q20=makeQuery(id+"F3.boolean.opBoolean","MERGE",EDGE,{"derivedFrom":[makeQuery(id+"F1.opExtrude","SWEPT_EDGE",EDGE,{"disambiguationData":[OSD([sQuery(id+"F0.wireOp",EDGE,"E9.2.1"),sQuery(id+"F0.wireOp",EDGE,"E9.2.2")])]}),makeQuery(id+"F3.opExtrude","SWEPT_EDGE",EDGE,{"disambiguationData":[OSD([sQuery(id+"F2.wireOp",EDGE,"E31.2.0"),sQuery(id+"F2.wireOp",EDGE,"E31.2.7")])]})]});
            var Q21;
            Q21=makeQuery(id+"F3.boolean.opBoolean","MERGE",EDGE,{"derivedFrom":[makeQuery(id+"F1.opExtrude","SWEPT_EDGE",EDGE,{"disambiguationData":[OSD([sQuery(id+"F0.wireOp",EDGE,"E9.2.2"),sQuery(id+"F0.wireOp",EDGE,"E9.2.3")])]}),makeQuery(id+"F3.opExtrude","SWEPT_EDGE",EDGE,{"disambiguationData":[OSD([sQuery(id+"F2.wireOp",EDGE,"E31.2.0"),sQuery(id+"F2.wireOp",EDGE,"E31.2.2")])]})]});
            var Q22;
            Q22=makeQuery(id+"F3.boolean.opBoolean","MERGE",EDGE,{"derivedFrom":[makeQuery(id+"F1.opExtrude","SWEPT_EDGE",EDGE,{"disambiguationData":[OSD([sQuery(id+"F0.wireOp",EDGE,"E9.2.4"),sQuery(id+"F0.wireOp",EDGE,"E9.2.5")])]}),makeQuery(id+"F3.opExtrude","SWEPT_EDGE",EDGE,{"disambiguationData":[OSD([sQuery(id+"F2.wireOp",EDGE,"E31.2.5"),sQuery(id+"F2.wireOp",EDGE,"E31.2.6")])]})]});
            var Q23;
            Q23=makeQuery(id+"F3.boolean.opBoolean","MERGE",EDGE,{"derivedFrom":[makeQuery(id+"F1.opExtrude","SWEPT_EDGE",EDGE,{"disambiguationData":[OSD([sQuery(id+"F0.wireOp",EDGE,"E9.2.3"),sQuery(id+"F0.wireOp",EDGE,"E9.2.6")])]}),makeQuery(id+"F3.opExtrude","SWEPT_EDGE",EDGE,{"disambiguationData":[OSD([sQuery(id+"F2.wireOp",EDGE,"E31.2.2"),sQuery(id+"F2.wireOp",EDGE,"E31.2.6")])]})]});
            var Q24;
            Q24=makeQuery(id+"F6.opExtrude","SWEPT_EDGE",EDGE,{"disambiguationData":[OSD([sQuery(id+"F5.wireOp",EDGE,"E34.2.2"),sQuery(id+"F5.wireOp",EDGE,"E34.2.5")])]});
            var Q25;
            Q25=makeQuery(id+"F6.opExtrude","SWEPT_EDGE",EDGE,{"disambiguationData":[OSD([sQuery(id+"F5.wireOp",EDGE,"E34.2.0"),sQuery(id+"F5.wireOp",EDGE,"E34.2.2")])]});
            var Q26;
            Q26=makeQuery(id+"F6.opExtrude","SWEPT_EDGE",EDGE,{"disambiguationData":[OSD([sQuery(id+"F5.wireOp",EDGE,"E34.2.5"),sQuery(id+"F5.wireOp",EDGE,"E34.2.6")])]});
            var Q27;
            Q27=makeQuery(id+"F6.opExtrude","SWEPT_EDGE",EDGE,{"disambiguationData":[OSD([sQuery(id+"F5.wireOp",EDGE,"E34.2.6"),sQuery(id+"F5.wireOp",EDGE,"E34.2.7")])]});
            var Q28;
            Q28=makeQuery(id+"F6.opExtrude","SWEPT_EDGE",EDGE,{"disambiguationData":[OSD([sQuery(id+"F5.wireOp",EDGE,"E34.2.1"),sQuery(id+"F5.wireOp",EDGE,"E34.2.7")])]});
            var Q29;
            Q29=makeQuery(id+"F6.opExtrude","SWEPT_EDGE",EDGE,{"disambiguationData":[OSD([sQuery(id+"F5.wireOp",EDGE,"E34.2.0"),sQuery(id+"F5.wireOp",EDGE,"E34.2.1")])]});
            var Q30;
            Q30=makeQuery(id+"F8.opExtrude","SWEPT_EDGE",EDGE,{"disambiguationData":[OSD([sQuery(id+"F7.wireOp",EDGE,"E37.2.1"),sQuery(id+"F7.wireOp",EDGE,"E37.2.5")])]});
            var Q31;
            Q31=makeQuery(id+"F8.opExtrude","SWEPT_EDGE",EDGE,{"disambiguationData":[OSD([sQuery(id+"F7.wireOp",EDGE,"E37.2.4"),sQuery(id+"F7.wireOp",EDGE,"E37.2.5")])]});
            var Q32;
            Q32=makeQuery(id+"F8.opExtrude","SWEPT_EDGE",EDGE,{"disambiguationData":[OSD([sQuery(id+"F7.wireOp",EDGE,"E37.2.4"),sQuery(id+"F7.wireOp",EDGE,"E37.2.6")])]});
            var Q33;
            Q33=makeQuery(id+"F8.opExtrude","SWEPT_EDGE",EDGE,{"disambiguationData":[OSD([sQuery(id+"F7.wireOp",EDGE,"E37.2.3"),sQuery(id+"F7.wireOp",EDGE,"E37.2.6")])]});
            var Q34;
            Q34=makeQuery(id+"F8.opExtrude","SWEPT_EDGE",EDGE,{"disambiguationData":[OSD([sQuery(id+"F7.wireOp",EDGE,"E37.2.2"),sQuery(id+"F7.wireOp",EDGE,"E37.2.3")])]});
            var Q35;
            Q35=makeQuery(id+"F8.opExtrude","SWEPT_EDGE",EDGE,{"disambiguationData":[OSD([sQuery(id+"F7.wireOp",EDGE,"E37.2.1"),sQuery(id+"F7.wireOp",EDGE,"E37.2.2")])]});
            var Q36;
            Q36=makeQuery(id+"F3.boolean.opBoolean","MERGE",EDGE,{"derivedFrom":[makeQuery(id+"F1.opExtrude","SWEPT_EDGE",EDGE,{"disambiguationData":[OSD([sQuery(id+"F0.wireOp",EDGE,"E10.0"),sQuery(id+"F0.wireOp",EDGE,"E24.trimOffspring")])]}),makeQuery(id+"F3.opExtrude","SWEPT_EDGE",EDGE,{"disambiguationData":[OSD([sQuery(id+"F2.wireOp",EDGE,"E29.2"),sQuery(id+"F2.wireOp",EDGE,"E29.3")])]})]});
            var Q37;
            Q37=makeQuery(id+"F3.boolean.opBoolean","MERGE",EDGE,{"derivedFrom":[makeQuery(id+"F1.opExtrude","SWEPT_EDGE",EDGE,{"disambiguationData":[OSD([sQuery(id+"F0.wireOp",EDGE,"E10.1"),sQuery(id+"F0.wireOp",EDGE,"E21.trimOffspring")])]}),makeQuery(id+"F3.opExtrude","SWEPT_EDGE",EDGE,{"disambiguationData":[OSD([sQuery(id+"F2.wireOp",EDGE,"E29.3"),sQuery(id+"F2.wireOp",EDGE,"E29.4")])]})]});
            var Q38;
            Q38=makeQuery(id+"F3.boolean.opBoolean","MERGE",EDGE,{"derivedFrom":[makeQuery(id+"F1.opExtrude","SWEPT_EDGE",EDGE,{"disambiguationData":[OSD([sQuery(id+"F0.wireOp",EDGE,"E10.5"),sQuery(id+"F0.wireOp",EDGE,"E27.trimOffspring")])]}),makeQuery(id+"F3.opExtrude","SWEPT_EDGE",EDGE,{"disambiguationData":[OSD([sQuery(id+"F2.wireOp",EDGE,"E29.1"),sQuery(id+"F2.wireOp",EDGE,"E29.2")])]})]});
            var Q39;
            Q39=makeQuery(id+"F3.boolean.opBoolean","MERGE",EDGE,{"derivedFrom":[makeQuery(id+"F1.opExtrude","SWEPT_EDGE",EDGE,{"disambiguationData":[OSD([sQuery(id+"F0.wireOp",EDGE,"E10.2"),sQuery(id+"F0.wireOp",EDGE,"E17.trimOffspring")])]}),makeQuery(id+"F3.opExtrude","SWEPT_EDGE",EDGE,{"disambiguationData":[OSD([sQuery(id+"F2.wireOp",EDGE,"E29.4"),sQuery(id+"F2.wireOp",EDGE,"E29.5")])]})]});
            var Q40;
            Q40=makeQuery(id+"F3.boolean.opBoolean","MERGE",EDGE,{"derivedFrom":[makeQuery(id+"F1.opExtrude","SWEPT_EDGE",EDGE,{"disambiguationData":[OSD([sQuery(id+"F0.wireOp",EDGE,"E10.3"),sQuery(id+"F0.wireOp",EDGE,"E15.trimOffspring")])]}),makeQuery(id+"F3.opExtrude","SWEPT_EDGE",EDGE,{"disambiguationData":[OSD([sQuery(id+"F2.wireOp",EDGE,"E29.0"),sQuery(id+"F2.wireOp",EDGE,"E29.5")])]})]});
            var Q41;
            Q41=makeQuery(id+"F3.boolean.opBoolean","MERGE",EDGE,{"derivedFrom":[makeQuery(id+"F1.opExtrude","SWEPT_EDGE",EDGE,{"disambiguationData":[OSD([sQuery(id+"F0.wireOp",EDGE,"E10.4"),sQuery(id+"F0.wireOp",EDGE,"E11.trimOffspring")])]}),makeQuery(id+"F3.opExtrude","SWEPT_EDGE",EDGE,{"disambiguationData":[OSD([sQuery(id+"F2.wireOp",EDGE,"E29.0"),sQuery(id+"F2.wireOp",EDGE,"E29.1")])]})]});
            var Q42;
            Q42=makeQuery(id+"F6.opExtrude","SWEPT_EDGE",EDGE,{"disambiguationData":[OSD([sQuery(id+"F5.wireOp",EDGE,"E32.0"),sQuery(id+"F5.wireOp",EDGE,"E32.5")])]});
            var Q43;
            Q43=makeQuery(id+"F6.opExtrude","SWEPT_EDGE",EDGE,{"disambiguationData":[OSD([sQuery(id+"F5.wireOp",EDGE,"E32.4"),sQuery(id+"F5.wireOp",EDGE,"E32.5")])]});
            var Q44;
            Q44=makeQuery(id+"F6.opExtrude","SWEPT_EDGE",EDGE,{"disambiguationData":[OSD([sQuery(id+"F5.wireOp",EDGE,"E32.3"),sQuery(id+"F5.wireOp",EDGE,"E32.4")])]});
            var Q45;
            Q45=makeQuery(id+"F6.opExtrude","SWEPT_EDGE",EDGE,{"disambiguationData":[OSD([sQuery(id+"F5.wireOp",EDGE,"E32.2"),sQuery(id+"F5.wireOp",EDGE,"E32.3")])]});
            var Q46;
            Q46=makeQuery(id+"F6.opExtrude","SWEPT_EDGE",EDGE,{"disambiguationData":[OSD([sQuery(id+"F5.wireOp",EDGE,"E32.1"),sQuery(id+"F5.wireOp",EDGE,"E32.2")])]});
            var Q47;
            Q47=makeQuery(id+"F6.opExtrude","SWEPT_EDGE",EDGE,{"disambiguationData":[OSD([sQuery(id+"F5.wireOp",EDGE,"E32.0"),sQuery(id+"F5.wireOp",EDGE,"E32.1")])]});
            var Q48;
            Q48=makeQuery(id+"F8.opExtrude","SWEPT_EDGE",EDGE,{"disambiguationData":[OSD([sQuery(id+"F7.wireOp",EDGE,"E35.0"),sQuery(id+"F7.wireOp",EDGE,"E35.1")])]});
            var Q49;
            Q49=makeQuery(id+"F8.opExtrude","SWEPT_EDGE",EDGE,{"disambiguationData":[OSD([sQuery(id+"F7.wireOp",EDGE,"E35.1"),sQuery(id+"F7.wireOp",EDGE,"E35.2")])]});
            var Q50;
            Q50=makeQuery(id+"F8.opExtrude","SWEPT_EDGE",EDGE,{"disambiguationData":[OSD([sQuery(id+"F7.wireOp",EDGE,"E35.2"),sQuery(id+"F7.wireOp",EDGE,"E35.3")])]});
            var Q51;
            Q51=makeQuery(id+"F8.opExtrude","SWEPT_EDGE",EDGE,{"disambiguationData":[OSD([sQuery(id+"F7.wireOp",EDGE,"E35.3"),sQuery(id+"F7.wireOp",EDGE,"E35.4")])]});
            var Q52;
            Q52=makeQuery(id+"F8.opExtrude","SWEPT_EDGE",EDGE,{"disambiguationData":[OSD([sQuery(id+"F7.wireOp",EDGE,"E35.4"),sQuery(id+"F7.wireOp",EDGE,"E35.5")])]});
            var Q53;
            Q53=makeQuery(id+"F8.opExtrude","SWEPT_EDGE",EDGE,{"disambiguationData":[OSD([sQuery(id+"F7.wireOp",EDGE,"E35.0"),sQuery(id+"F7.wireOp",EDGE,"E35.5")])]});
            var Q54;
            Q54=makeQuery(id+"F3.boolean.opBoolean","MERGE",EDGE,{"derivedFrom":[makeQuery(id+"F1.opExtrude","SWEPT_EDGE",EDGE,{"disambiguationData":[OSD([sQuery(id+"F0.wireOp",EDGE,"E9.4.3"),sQuery(id+"F0.wireOp",EDGE,"E9.4.6")])]}),makeQuery(id+"F3.opExtrude","SWEPT_EDGE",EDGE,{"disambiguationData":[OSD([sQuery(id+"F2.wireOp",EDGE,"E31.4.2"),sQuery(id+"F2.wireOp",EDGE,"E31.4.6")])]})]});
            var Q55;
            Q55=makeQuery(id+"F3.boolean.opBoolean","MERGE",EDGE,{"derivedFrom":[makeQuery(id+"F1.opExtrude","SWEPT_EDGE",EDGE,{"disambiguationData":[OSD([sQuery(id+"F0.wireOp",EDGE,"E9.4.4"),sQuery(id+"F0.wireOp",EDGE,"E9.4.5")])]}),makeQuery(id+"F3.opExtrude","SWEPT_EDGE",EDGE,{"disambiguationData":[OSD([sQuery(id+"F2.wireOp",EDGE,"E31.4.5"),sQuery(id+"F2.wireOp",EDGE,"E31.4.6")])]})]});
            var Q56;
            Q56=makeQuery(id+"F3.boolean.opBoolean","MERGE",EDGE,{"derivedFrom":[makeQuery(id+"F1.opExtrude","SWEPT_EDGE",EDGE,{"disambiguationData":[OSD([sQuery(id+"F0.wireOp",EDGE,"E9.4.0"),sQuery(id+"F0.wireOp",EDGE,"E9.4.4")])]}),makeQuery(id+"F3.opExtrude","SWEPT_EDGE",EDGE,{"disambiguationData":[OSD([sQuery(id+"F2.wireOp",EDGE,"E31.4.3"),sQuery(id+"F2.wireOp",EDGE,"E31.4.5")])]})]});
            var Q57;
            Q57=makeQuery(id+"F3.boolean.opBoolean","MERGE",EDGE,{"derivedFrom":[makeQuery(id+"F1.opExtrude","SWEPT_EDGE",EDGE,{"disambiguationData":[OSD([sQuery(id+"F0.wireOp",EDGE,"E9.4.0"),sQuery(id+"F0.wireOp",EDGE,"E9.4.1")])]}),makeQuery(id+"F3.opExtrude","SWEPT_EDGE",EDGE,{"disambiguationData":[OSD([sQuery(id+"F2.wireOp",EDGE,"E31.4.3"),sQuery(id+"F2.wireOp",EDGE,"E31.4.7")])]})]});
            var Q58;
            Q58=makeQuery(id+"F3.boolean.opBoolean","MERGE",EDGE,{"derivedFrom":[makeQuery(id+"F1.opExtrude","SWEPT_EDGE",EDGE,{"disambiguationData":[OSD([sQuery(id+"F0.wireOp",EDGE,"E9.4.1"),sQuery(id+"F0.wireOp",EDGE,"E9.4.2")])]}),makeQuery(id+"F3.opExtrude","SWEPT_EDGE",EDGE,{"disambiguationData":[OSD([sQuery(id+"F2.wireOp",EDGE,"E31.4.0"),sQuery(id+"F2.wireOp",EDGE,"E31.4.7")])]})]});
            var Q59;
            Q59=makeQuery(id+"F3.boolean.opBoolean","MERGE",EDGE,{"derivedFrom":[makeQuery(id+"F1.opExtrude","SWEPT_EDGE",EDGE,{"disambiguationData":[OSD([sQuery(id+"F0.wireOp",EDGE,"E9.4.2"),sQuery(id+"F0.wireOp",EDGE,"E9.4.3")])]}),makeQuery(id+"F3.opExtrude","SWEPT_EDGE",EDGE,{"disambiguationData":[OSD([sQuery(id+"F2.wireOp",EDGE,"E31.4.0"),sQuery(id+"F2.wireOp",EDGE,"E31.4.2")])]})]});
            var Q60;
            Q60=makeQuery(id+"F6.opExtrude","SWEPT_EDGE",EDGE,{"disambiguationData":[OSD([sQuery(id+"F5.wireOp",EDGE,"E34.4.0"),sQuery(id+"F5.wireOp",EDGE,"E34.4.1")])]});
            var Q61;
            Q61=makeQuery(id+"F6.opExtrude","SWEPT_EDGE",EDGE,{"disambiguationData":[OSD([sQuery(id+"F5.wireOp",EDGE,"E34.4.1"),sQuery(id+"F5.wireOp",EDGE,"E34.4.7")])]});
            var Q62;
            Q62=makeQuery(id+"F6.opExtrude","SWEPT_EDGE",EDGE,{"disambiguationData":[OSD([sQuery(id+"F5.wireOp",EDGE,"E34.4.6"),sQuery(id+"F5.wireOp",EDGE,"E34.4.7")])]});
            var Q63;
            Q63=makeQuery(id+"F6.opExtrude","SWEPT_EDGE",EDGE,{"disambiguationData":[OSD([sQuery(id+"F5.wireOp",EDGE,"E34.4.0"),sQuery(id+"F5.wireOp",EDGE,"E34.4.2")])]});
            var Q64;
            Q64=makeQuery(id+"F6.opExtrude","SWEPT_EDGE",EDGE,{"disambiguationData":[OSD([sQuery(id+"F5.wireOp",EDGE,"E34.4.2"),sQuery(id+"F5.wireOp",EDGE,"E34.4.5")])]});
            var Q65;
            Q65=makeQuery(id+"F6.opExtrude","SWEPT_EDGE",EDGE,{"disambiguationData":[OSD([sQuery(id+"F5.wireOp",EDGE,"E34.4.5"),sQuery(id+"F5.wireOp",EDGE,"E34.4.6")])]});
            var Q66;
            Q66=makeQuery(id+"F8.opExtrude","SWEPT_EDGE",EDGE,{"disambiguationData":[OSD([sQuery(id+"F7.wireOp",EDGE,"E37.4.4"),sQuery(id+"F7.wireOp",EDGE,"E37.4.6")])]});
            var Q67;
            Q67=makeQuery(id+"F8.opExtrude","SWEPT_EDGE",EDGE,{"disambiguationData":[OSD([sQuery(id+"F7.wireOp",EDGE,"E37.4.1"),sQuery(id+"F7.wireOp",EDGE,"E37.4.5")])]});
            var Q68;
            Q68=makeQuery(id+"F8.opExtrude","SWEPT_EDGE",EDGE,{"disambiguationData":[OSD([sQuery(id+"F7.wireOp",EDGE,"E37.4.4"),sQuery(id+"F7.wireOp",EDGE,"E37.4.5")])]});
            var Q69;
            Q69=makeQuery(id+"F8.opExtrude","SWEPT_EDGE",EDGE,{"disambiguationData":[OSD([sQuery(id+"F7.wireOp",EDGE,"E37.4.2"),sQuery(id+"F7.wireOp",EDGE,"E37.4.3")])]});
            var Q70;
            Q70=makeQuery(id+"F8.opExtrude","SWEPT_EDGE",EDGE,{"disambiguationData":[OSD([sQuery(id+"F7.wireOp",EDGE,"E37.4.1"),sQuery(id+"F7.wireOp",EDGE,"E37.4.2")])]});
            var Q71;
            Q71=makeQuery(id+"F8.opExtrude","SWEPT_EDGE",EDGE,{"disambiguationData":[OSD([sQuery(id+"F7.wireOp",EDGE,"E37.4.3"),sQuery(id+"F7.wireOp",EDGE,"E37.4.6")])]});
            var Q72;
            Q72=makeQuery(id+"F3.boolean.opBoolean","MERGE",EDGE,{"derivedFrom":[makeQuery(id+"F1.opExtrude","SWEPT_EDGE",EDGE,{"disambiguationData":[OSD([sQuery(id+"F0.wireOp",EDGE,"E9.5.3"),sQuery(id+"F0.wireOp",EDGE,"E9.5.6")])]}),makeQuery(id+"F3.opExtrude","SWEPT_EDGE",EDGE,{"disambiguationData":[OSD([sQuery(id+"F2.wireOp",EDGE,"E31.5.2"),sQuery(id+"F2.wireOp",EDGE,"E31.5.6")])]})]});
            var Q73;
            Q73=makeQuery(id+"F3.boolean.opBoolean","MERGE",EDGE,{"derivedFrom":[makeQuery(id+"F1.opExtrude","SWEPT_EDGE",EDGE,{"disambiguationData":[OSD([sQuery(id+"F0.wireOp",EDGE,"E9.5.2"),sQuery(id+"F0.wireOp",EDGE,"E9.5.3")])]}),makeQuery(id+"F3.opExtrude","SWEPT_EDGE",EDGE,{"disambiguationData":[OSD([sQuery(id+"F2.wireOp",EDGE,"E31.5.0"),sQuery(id+"F2.wireOp",EDGE,"E31.5.2")])]})]});
            var Q74;
            Q74=makeQuery(id+"F3.boolean.opBoolean","MERGE",EDGE,{"derivedFrom":[makeQuery(id+"F1.opExtrude","SWEPT_EDGE",EDGE,{"disambiguationData":[OSD([sQuery(id+"F0.wireOp",EDGE,"E9.5.1"),sQuery(id+"F0.wireOp",EDGE,"E9.5.2")])]}),makeQuery(id+"F3.opExtrude","SWEPT_EDGE",EDGE,{"disambiguationData":[OSD([sQuery(id+"F2.wireOp",EDGE,"E31.5.0"),sQuery(id+"F2.wireOp",EDGE,"E31.5.7")])]})]});
            var Q75;
            Q75=makeQuery(id+"F3.boolean.opBoolean","MERGE",EDGE,{"derivedFrom":[makeQuery(id+"F1.opExtrude","SWEPT_EDGE",EDGE,{"disambiguationData":[OSD([sQuery(id+"F0.wireOp",EDGE,"E9.5.0"),sQuery(id+"F0.wireOp",EDGE,"E9.5.1")])]}),makeQuery(id+"F3.opExtrude","SWEPT_EDGE",EDGE,{"disambiguationData":[OSD([sQuery(id+"F2.wireOp",EDGE,"E31.5.3"),sQuery(id+"F2.wireOp",EDGE,"E31.5.7")])]})]});
            var Q76;
            Q76=makeQuery(id+"F3.boolean.opBoolean","MERGE",EDGE,{"derivedFrom":[makeQuery(id+"F1.opExtrude","SWEPT_EDGE",EDGE,{"disambiguationData":[OSD([sQuery(id+"F0.wireOp",EDGE,"E9.5.0"),sQuery(id+"F0.wireOp",EDGE,"E9.5.4")])]}),makeQuery(id+"F3.opExtrude","SWEPT_EDGE",EDGE,{"disambiguationData":[OSD([sQuery(id+"F2.wireOp",EDGE,"E31.5.3"),sQuery(id+"F2.wireOp",EDGE,"E31.5.5")])]})]});
            var Q77;
            Q77=makeQuery(id+"F3.boolean.opBoolean","MERGE",EDGE,{"derivedFrom":[makeQuery(id+"F1.opExtrude","SWEPT_EDGE",EDGE,{"disambiguationData":[OSD([sQuery(id+"F0.wireOp",EDGE,"E9.5.4"),sQuery(id+"F0.wireOp",EDGE,"E9.5.5")])]}),makeQuery(id+"F3.opExtrude","SWEPT_EDGE",EDGE,{"disambiguationData":[OSD([sQuery(id+"F2.wireOp",EDGE,"E31.5.5"),sQuery(id+"F2.wireOp",EDGE,"E31.5.6")])]})]});
            var Q78;
            Q78=makeQuery(id+"F6.opExtrude","SWEPT_EDGE",EDGE,{"disambiguationData":[OSD([sQuery(id+"F5.wireOp",EDGE,"E34.5.0"),sQuery(id+"F5.wireOp",EDGE,"E34.5.2")])]});
            var Q79;
            Q79=makeQuery(id+"F6.opExtrude","SWEPT_EDGE",EDGE,{"disambiguationData":[OSD([sQuery(id+"F5.wireOp",EDGE,"E34.5.2"),sQuery(id+"F5.wireOp",EDGE,"E34.5.5")])]});
            var Q80;
            Q80=makeQuery(id+"F6.opExtrude","SWEPT_EDGE",EDGE,{"disambiguationData":[OSD([sQuery(id+"F5.wireOp",EDGE,"E34.5.5"),sQuery(id+"F5.wireOp",EDGE,"E34.5.6")])]});
            var Q81;
            Q81=makeQuery(id+"F8.opExtrude","SWEPT_EDGE",EDGE,{"disambiguationData":[OSD([sQuery(id+"F7.wireOp",EDGE,"E37.5.2"),sQuery(id+"F7.wireOp",EDGE,"E37.5.3")])]});
            var Q82;
            Q82=makeQuery(id+"F8.opExtrude","SWEPT_EDGE",EDGE,{"disambiguationData":[OSD([sQuery(id+"F7.wireOp",EDGE,"E37.5.3"),sQuery(id+"F7.wireOp",EDGE,"E37.5.6")])]});
            var Q83;
            Q83=makeQuery(id+"F8.opExtrude","SWEPT_EDGE",EDGE,{"disambiguationData":[OSD([sQuery(id+"F7.wireOp",EDGE,"E37.5.4"),sQuery(id+"F7.wireOp",EDGE,"E37.5.6")])]});
            var Q84;
            Q84=makeQuery(id+"F6.opExtrude","SWEPT_EDGE",EDGE,{"disambiguationData":[OSD([sQuery(id+"F5.wireOp",EDGE,"E34.5.0"),sQuery(id+"F5.wireOp",EDGE,"E34.5.1")])]});
            var Q85;
            Q85=makeQuery(id+"F8.opExtrude","SWEPT_EDGE",EDGE,{"disambiguationData":[OSD([sQuery(id+"F7.wireOp",EDGE,"E37.5.1"),sQuery(id+"F7.wireOp",EDGE,"E37.5.2")])]});
            var Q86;
            Q86=makeQuery(id+"F8.opExtrude","SWEPT_EDGE",EDGE,{"disambiguationData":[OSD([sQuery(id+"F7.wireOp",EDGE,"E37.5.1"),sQuery(id+"F7.wireOp",EDGE,"E37.5.5")])]});
            var Q87;
            Q87=makeQuery(id+"F6.opExtrude","SWEPT_EDGE",EDGE,{"disambiguationData":[OSD([sQuery(id+"F5.wireOp",EDGE,"E34.5.1"),sQuery(id+"F5.wireOp",EDGE,"E34.5.7")])]});
            var Q88;
            Q88=makeQuery(id+"F8.opExtrude","SWEPT_EDGE",EDGE,{"disambiguationData":[OSD([sQuery(id+"F7.wireOp",EDGE,"E37.5.4"),sQuery(id+"F7.wireOp",EDGE,"E37.5.5")])]});
            var Q89;
            Q89=makeQuery(id+"F6.opExtrude","SWEPT_EDGE",EDGE,{"disambiguationData":[OSD([sQuery(id+"F5.wireOp",EDGE,"E34.5.6"),sQuery(id+"F5.wireOp",EDGE,"E34.5.7")])]});
            var Q90;
            Q90=makeQuery(id+"F3.boolean.opBoolean","MERGE",EDGE,{"derivedFrom":[makeQuery(id+"F1.opExtrude","SWEPT_EDGE",EDGE,{"disambiguationData":[OSD([sQuery(id+"F0.wireOp",EDGE,"E9.1.4"),sQuery(id+"F0.wireOp",EDGE,"E9.1.5")])]}),makeQuery(id+"F3.opExtrude","SWEPT_EDGE",EDGE,{"disambiguationData":[OSD([sQuery(id+"F2.wireOp",EDGE,"E31.1.5"),sQuery(id+"F2.wireOp",EDGE,"E31.1.6")])]})]});
            var Q91;
            Q91=makeQuery(id+"F3.boolean.opBoolean","MERGE",EDGE,{"derivedFrom":[makeQuery(id+"F1.opExtrude","SWEPT_EDGE",EDGE,{"disambiguationData":[OSD([sQuery(id+"F0.wireOp",EDGE,"E9.1.3"),sQuery(id+"F0.wireOp",EDGE,"E9.1.6")])]}),makeQuery(id+"F3.opExtrude","SWEPT_EDGE",EDGE,{"disambiguationData":[OSD([sQuery(id+"F2.wireOp",EDGE,"E31.1.2"),sQuery(id+"F2.wireOp",EDGE,"E31.1.6")])]})]});
            var Q92;
            Q92=makeQuery(id+"F6.opExtrude","SWEPT_EDGE",EDGE,{"disambiguationData":[OSD([sQuery(id+"F5.wireOp",EDGE,"E34.1.2"),sQuery(id+"F5.wireOp",EDGE,"E34.1.5")])]});
            var Q93;
            Q93=makeQuery(id+"F6.opExtrude","SWEPT_EDGE",EDGE,{"disambiguationData":[OSD([sQuery(id+"F5.wireOp",EDGE,"E34.1.0"),sQuery(id+"F5.wireOp",EDGE,"E34.1.2")])]});
            var Q94;
            Q94=makeQuery(id+"F6.opExtrude","SWEPT_EDGE",EDGE,{"disambiguationData":[OSD([sQuery(id+"F5.wireOp",EDGE,"E34.1.0"),sQuery(id+"F5.wireOp",EDGE,"E34.1.1")])]});
            var Q95;
            Q95=makeQuery(id+"F3.boolean.opBoolean","MERGE",EDGE,{"derivedFrom":[makeQuery(id+"F1.opExtrude","SWEPT_EDGE",EDGE,{"disambiguationData":[OSD([sQuery(id+"F0.wireOp",EDGE,"E9.1.2"),sQuery(id+"F0.wireOp",EDGE,"E9.1.3")])]}),makeQuery(id+"F3.opExtrude","SWEPT_EDGE",EDGE,{"disambiguationData":[OSD([sQuery(id+"F2.wireOp",EDGE,"E31.1.0"),sQuery(id+"F2.wireOp",EDGE,"E31.1.2")])]})]});
            var Q96;
            Q96=makeQuery(id+"F8.opExtrude","SWEPT_EDGE",EDGE,{"disambiguationData":[OSD([sQuery(id+"F7.wireOp",EDGE,"E37.1.2"),sQuery(id+"F7.wireOp",EDGE,"E37.1.3")])]});
            var Q97;
            Q97=makeQuery(id+"F8.opExtrude","SWEPT_EDGE",EDGE,{"disambiguationData":[OSD([sQuery(id+"F7.wireOp",EDGE,"E37.1.1"),sQuery(id+"F7.wireOp",EDGE,"E37.1.2")])]});
            var Q98;
            Q98=makeQuery(id+"F8.opExtrude","SWEPT_EDGE",EDGE,{"disambiguationData":[OSD([sQuery(id+"F7.wireOp",EDGE,"E37.1.3"),sQuery(id+"F7.wireOp",EDGE,"E37.1.6")])]});
            var Q99;
            Q99=makeQuery(id+"F3.boolean.opBoolean","MERGE",EDGE,{"derivedFrom":[makeQuery(id+"F1.opExtrude","SWEPT_EDGE",EDGE,{"disambiguationData":[OSD([sQuery(id+"F0.wireOp",EDGE,"E9.1.0"),sQuery(id+"F0.wireOp",EDGE,"E9.1.4")])]}),makeQuery(id+"F3.opExtrude","SWEPT_EDGE",EDGE,{"disambiguationData":[OSD([sQuery(id+"F2.wireOp",EDGE,"E31.1.3"),sQuery(id+"F2.wireOp",EDGE,"E31.1.5")])]})]});
            var Q100;
            Q100=makeQuery(id+"F6.opExtrude","SWEPT_EDGE",EDGE,{"disambiguationData":[OSD([sQuery(id+"F5.wireOp",EDGE,"E34.1.5"),sQuery(id+"F5.wireOp",EDGE,"E34.1.6")])]});
            var Q101;
            Q101=makeQuery(id+"F8.opExtrude","SWEPT_EDGE",EDGE,{"disambiguationData":[OSD([sQuery(id+"F7.wireOp",EDGE,"E37.1.4"),sQuery(id+"F7.wireOp",EDGE,"E37.1.6")])]});
            var Q102;
            Q102=makeQuery(id+"F8.opExtrude","SWEPT_EDGE",EDGE,{"disambiguationData":[OSD([sQuery(id+"F7.wireOp",EDGE,"E37.1.1"),sQuery(id+"F7.wireOp",EDGE,"E37.1.5")])]});
            var Q103;
            Q103=makeQuery(id+"F6.opExtrude","SWEPT_EDGE",EDGE,{"disambiguationData":[OSD([sQuery(id+"F5.wireOp",EDGE,"E34.1.1"),sQuery(id+"F5.wireOp",EDGE,"E34.1.7")])]});
            var Q104;
            Q104=makeQuery(id+"F3.boolean.opBoolean","MERGE",EDGE,{"derivedFrom":[makeQuery(id+"F1.opExtrude","SWEPT_EDGE",EDGE,{"disambiguationData":[OSD([sQuery(id+"F0.wireOp",EDGE,"E9.1.1"),sQuery(id+"F0.wireOp",EDGE,"E9.1.2")])]}),makeQuery(id+"F3.opExtrude","SWEPT_EDGE",EDGE,{"disambiguationData":[OSD([sQuery(id+"F2.wireOp",EDGE,"E31.1.0"),sQuery(id+"F2.wireOp",EDGE,"E31.1.7")])]})]});
            var Q105;
            Q105=makeQuery(id+"F8.opExtrude","SWEPT_EDGE",EDGE,{"disambiguationData":[OSD([sQuery(id+"F7.wireOp",EDGE,"E37.1.4"),sQuery(id+"F7.wireOp",EDGE,"E37.1.5")])]});
            var Q106;
            Q106=makeQuery(id+"F6.opExtrude","SWEPT_EDGE",EDGE,{"disambiguationData":[OSD([sQuery(id+"F5.wireOp",EDGE,"E34.1.6"),sQuery(id+"F5.wireOp",EDGE,"E34.1.7")])]});
            var Q107;
            Q107=makeQuery(id+"F3.boolean.opBoolean","MERGE",EDGE,{"derivedFrom":[makeQuery(id+"F1.opExtrude","SWEPT_EDGE",EDGE,{"disambiguationData":[OSD([sQuery(id+"F0.wireOp",EDGE,"E9.1.0"),sQuery(id+"F0.wireOp",EDGE,"E9.1.1")])]}),makeQuery(id+"F3.opExtrude","SWEPT_EDGE",EDGE,{"disambiguationData":[OSD([sQuery(id+"F2.wireOp",EDGE,"E31.1.3"),sQuery(id+"F2.wireOp",EDGE,"E31.1.7")])]})]});
            var Q108;
            Q108=makeQuery(id+"F3.boolean.opBoolean","MERGE",EDGE,{"derivedFrom":[makeQuery(id+"F1.opExtrude","SWEPT_EDGE",EDGE,{"disambiguationData":[OSD([sQuery(id+"F0.wireOp",EDGE,"E7.2"),sQuery(id+"F0.wireOp",EDGE,"E7.3")])]}),makeQuery(id+"F3.opExtrude","SWEPT_EDGE",EDGE,{"disambiguationData":[OSD([sQuery(id+"F2.wireOp",EDGE,"E30.2"),sQuery(id+"F2.wireOp",EDGE,"E30.3")])]})]});
            var Q109;
            Q109=makeQuery(id+"F6.opExtrude","SWEPT_EDGE",EDGE,{"disambiguationData":[OSD([sQuery(id+"F5.wireOp",EDGE,"E33.2"),sQuery(id+"F5.wireOp",EDGE,"E33.3")])]});
            var Q110;
            Q110=makeQuery(id+"F8.opExtrude","SWEPT_EDGE",EDGE,{"disambiguationData":[OSD([sQuery(id+"F7.wireOp",EDGE,"E36.2"),sQuery(id+"F7.wireOp",EDGE,"E36.3")])]});
            var Q111;
            Q111=makeQuery(id+"F3.boolean.opBoolean","MERGE",EDGE,{"derivedFrom":[makeQuery(id+"F1.opExtrude","SWEPT_EDGE",EDGE,{"disambiguationData":[OSD([sQuery(id+"F0.wireOp",EDGE,"E7.1"),sQuery(id+"F0.wireOp",EDGE,"E7.2")])]}),makeQuery(id+"F3.opExtrude","SWEPT_EDGE",EDGE,{"disambiguationData":[OSD([sQuery(id+"F2.wireOp",EDGE,"E30.1"),sQuery(id+"F2.wireOp",EDGE,"E30.2")])]})]});
            var Q112;
            Q112=makeQuery(id+"F6.opExtrude","SWEPT_EDGE",EDGE,{"disambiguationData":[OSD([sQuery(id+"F5.wireOp",EDGE,"E33.1"),sQuery(id+"F5.wireOp",EDGE,"E33.2")])]});
            var Q113;
            Q113=makeQuery(id+"F8.opExtrude","SWEPT_EDGE",EDGE,{"disambiguationData":[OSD([sQuery(id+"F7.wireOp",EDGE,"E36.1"),sQuery(id+"F7.wireOp",EDGE,"E36.2")])]});
            var Q114;
            Q114=makeQuery(id+"F8.opExtrude","SWEPT_EDGE",EDGE,{"disambiguationData":[OSD([sQuery(id+"F7.wireOp",EDGE,"E36.0"),sQuery(id+"F7.wireOp",EDGE,"E36.1")])]});
            var Q115;
            Q115=makeQuery(id+"F6.opExtrude","SWEPT_EDGE",EDGE,{"disambiguationData":[OSD([sQuery(id+"F5.wireOp",EDGE,"E33.0"),sQuery(id+"F5.wireOp",EDGE,"E33.1")])]});
            var Q116;
            Q116=makeQuery(id+"F3.boolean.opBoolean","MERGE",EDGE,{"derivedFrom":[makeQuery(id+"F1.opExtrude","SWEPT_EDGE",EDGE,{"disambiguationData":[OSD([sQuery(id+"F0.wireOp",EDGE,"E7.0"),sQuery(id+"F0.wireOp",EDGE,"E7.1")])]}),makeQuery(id+"F3.opExtrude","SWEPT_EDGE",EDGE,{"disambiguationData":[OSD([sQuery(id+"F2.wireOp",EDGE,"E30.0"),sQuery(id+"F2.wireOp",EDGE,"E30.1")])]})]});
            var Q117;
            Q117=makeQuery(id+"F8.opExtrude","SWEPT_EDGE",EDGE,{"disambiguationData":[OSD([sQuery(id+"F7.wireOp",EDGE,"E36.0"),sQuery(id+"F7.wireOp",EDGE,"E36.5")])]});
            var Q118;
            Q118=makeQuery(id+"F6.opExtrude","SWEPT_EDGE",EDGE,{"disambiguationData":[OSD([sQuery(id+"F5.wireOp",EDGE,"E33.0"),sQuery(id+"F5.wireOp",EDGE,"E33.5")])]});
            var Q119;
            Q119=makeQuery(id+"F3.boolean.opBoolean","MERGE",EDGE,{"derivedFrom":[makeQuery(id+"F1.opExtrude","SWEPT_EDGE",EDGE,{"disambiguationData":[OSD([sQuery(id+"F0.wireOp",EDGE,"E7.0"),sQuery(id+"F0.wireOp",EDGE,"E7.5")])]}),makeQuery(id+"F3.opExtrude","SWEPT_EDGE",EDGE,{"disambiguationData":[OSD([sQuery(id+"F2.wireOp",EDGE,"E30.0"),sQuery(id+"F2.wireOp",EDGE,"E30.5")])]})]});
            var Q120;
            Q120=makeQuery(id+"F8.opExtrude","SWEPT_EDGE",EDGE,{"disambiguationData":[OSD([sQuery(id+"F7.wireOp",EDGE,"E36.4"),sQuery(id+"F7.wireOp",EDGE,"E36.5")])]});
            var Q121;
            Q121=makeQuery(id+"F6.opExtrude","SWEPT_EDGE",EDGE,{"disambiguationData":[OSD([sQuery(id+"F5.wireOp",EDGE,"E33.4"),sQuery(id+"F5.wireOp",EDGE,"E33.5")])]});
            var Q122;
            Q122=makeQuery(id+"F3.boolean.opBoolean","MERGE",EDGE,{"derivedFrom":[makeQuery(id+"F1.opExtrude","SWEPT_EDGE",EDGE,{"disambiguationData":[OSD([sQuery(id+"F0.wireOp",EDGE,"E7.4"),sQuery(id+"F0.wireOp",EDGE,"E7.5")])]}),makeQuery(id+"F3.opExtrude","SWEPT_EDGE",EDGE,{"disambiguationData":[OSD([sQuery(id+"F2.wireOp",EDGE,"E30.4"),sQuery(id+"F2.wireOp",EDGE,"E30.5")])]})]});
            var Q123;
            Q123=makeQuery(id+"F8.opExtrude","SWEPT_EDGE",EDGE,{"disambiguationData":[OSD([sQuery(id+"F7.wireOp",EDGE,"E36.3"),sQuery(id+"F7.wireOp",EDGE,"E36.4")])]});
            var Q124;
            Q124=makeQuery(id+"F6.opExtrude","SWEPT_EDGE",EDGE,{"disambiguationData":[OSD([sQuery(id+"F5.wireOp",EDGE,"E33.3"),sQuery(id+"F5.wireOp",EDGE,"E33.4")])]});
            var Q125;
            Q125=makeQuery(id+"F3.boolean.opBoolean","MERGE",EDGE,{"derivedFrom":[makeQuery(id+"F1.opExtrude","SWEPT_EDGE",EDGE,{"disambiguationData":[OSD([sQuery(id+"F0.wireOp",EDGE,"E7.4"),sQuery(id+"F0.wireOp",EDGE,"E8.trimOffspring")])]}),makeQuery(id+"F3.opExtrude","SWEPT_EDGE",EDGE,{"disambiguationData":[OSD([sQuery(id+"F2.wireOp",EDGE,"E30.3"),sQuery(id+"F2.wireOp",EDGE,"E30.4")])]})]});
            fillet(context, id + "F13", {"entities" : qUnion([Q0, Q1, Q2, Q3, Q4, Q5, Q6, Q7, Q8, Q9, Q10, Q11, Q12, Q13, Q14, Q15, Q16, Q17, Q18, Q19, Q20, Q21, Q22, Q23, Q24, Q25, Q26, Q27, Q28, Q29, Q30, Q31, Q32, Q33, Q34, Q35, Q36, Q37, Q38, Q39, Q40, Q41, Q42, Q43, Q44, Q45, Q46, Q47, Q48, Q49, Q50, Q51, Q52, Q53, Q54, Q55, Q56, Q57, Q58, Q59, Q60, Q61, Q62, Q63, Q64, Q65, Q66, Q67, Q68, Q69, Q70, Q71, Q72, Q73, Q74, Q75, Q76, Q77, Q78, Q79, Q80, Q81, Q82, Q83, Q84, Q85, Q86, Q87, Q88, Q89, Q90, Q91, Q92, Q93, Q94, Q95, Q96, Q97, Q98, Q99, Q100, Q101, Q102, Q103, Q104, Q105, Q106, Q107, Q108, Q109, Q110, Q111, Q112, Q113, Q114, Q115, Q116, Q117, Q118, Q119, Q120, Q121, Q122, Q123, Q124, Q125]), "radius" : 2.5 * mm, "tangentPropagation" : true, "allowEdgeOverflow" : false});
        }
        {
            var Q0;
            Q0=qCreatedBy(makeId("Front.planeOp"),FACE);
            var sketch = newSketch(context, id + "F14", { "sketchPlane" : qUnion([Q0])});
            skLineSegment(sketch, "E40.0", {"start": v(2.89, 16.5) * mm, "end": v(-2.89, 16.5) * mm, "construction": true});
            skLineSegment(sketch, "E41", {"start": v(0, 16.5) * mm, "end": v(0, 40.16) * mm, "construction": true});
            skSolve(sketch);
        }
        {
            var Q0;
            {var subQ0=sQuery(id+"F0.wireOp",EDGE,"E7.3");var subQ1=sQuery(id+"F0.wireOp",EDGE,"E11.trimOffspring");var subQ2=sQuery(id+"F0.wireOp",EDGE,"E5.right");var subQ3=sQuery(id+"F0.wireOp",EDGE,"E8.trimOffspring");var subQ4=sQuery(id+"F0.wireOp",EDGE,"E5.left");var subQ5=sQuery(id+"F0.wireOp",EDGE,"E10.3");Q0=makeQuery(id+"F3.boolean.opBoolean","SPLIT",FACE,{"disambiguationData":[TD([makeQuery(id+"F1.opExtrude","SWEPT_FACE",FACE,{"disambiguationData":[OSD([subQ4])]})])],"derivedFrom":makeQuery(id+"F1.opExtrude","CAP_FACE",FACE,{"disambiguationData":[OSD([subQ4,subQ2,sQuery(id+"F0.wireOp",EDGE,"E7.0"),sQuery(id+"F0.wireOp",EDGE,"E7.1"),sQuery(id+"F0.wireOp",EDGE,"E7.2"),subQ0,sQuery(id+"F0.wireOp",EDGE,"E7.4"),sQuery(id+"F0.wireOp",EDGE,"E7.5"),subQ3,sQuery(id+"F0.wireOp",EDGE,"E9.1.0"),sQuery(id+"F0.wireOp",EDGE,"E9.1.1"),sQuery(id+"F0.wireOp",EDGE,"E9.1.2"),sQuery(id+"F0.wireOp",EDGE,"E9.1.3"),sQuery(id+"F0.wireOp",EDGE,"E9.1.4"),sQuery(id+"F0.wireOp",EDGE,"E9.1.5"),sQuery(id+"F0.wireOp",EDGE,"E9.1.6"),sQuery(id+"F0.wireOp",EDGE,"E9.1.7"),sQuery(id+"F0.wireOp",EDGE,"E9.1.8"),sQuery(id+"F0.wireOp",EDGE,"E9.2.0"),sQuery(id+"F0.wireOp",EDGE,"E9.2.1"),sQuery(id+"F0.wireOp",EDGE,"E9.2.2"),sQuery(id+"F0.wireOp",EDGE,"E9.2.3"),sQuery(id+"F0.wireOp",EDGE,"E9.2.4"),sQuery(id+"F0.wireOp",EDGE,"E9.2.5"),sQuery(id+"F0.wireOp",EDGE,"E9.2.6"),sQuery(id+"F0.wireOp",EDGE,"E9.2.7"),sQuery(id+"F0.wireOp",EDGE,"E9.2.8"),sQuery(id+"F0.wireOp",EDGE,"E9.3.0"),sQuery(id+"F0.wireOp",EDGE,"E9.3.1"),sQuery(id+"F0.wireOp",EDGE,"E9.3.2"),sQuery(id+"F0.wireOp",EDGE,"E9.3.3"),sQuery(id+"F0.wireOp",EDGE,"E9.3.4"),sQuery(id+"F0.wireOp",EDGE,"E9.3.5"),sQuery(id+"F0.wireOp",EDGE,"E9.3.6"),sQuery(id+"F0.wireOp",EDGE,"E9.3.7"),sQuery(id+"F0.wireOp",EDGE,"E9.3.8"),sQuery(id+"F0.wireOp",EDGE,"E9.4.0"),sQuery(id+"F0.wireOp",EDGE,"E9.4.1"),sQuery(id+"F0.wireOp",EDGE,"E9.4.2"),sQuery(id+"F0.wireOp",EDGE,"E9.4.3"),sQuery(id+"F0.wireOp",EDGE,"E9.4.4"),sQuery(id+"F0.wireOp",EDGE,"E9.4.5"),sQuery(id+"F0.wireOp",EDGE,"E9.4.6"),sQuery(id+"F0.wireOp",EDGE,"E9.4.7"),sQuery(id+"F0.wireOp",EDGE,"E9.4.8"),sQuery(id+"F0.wireOp",EDGE,"E9.5.0"),sQuery(id+"F0.wireOp",EDGE,"E9.5.1"),sQuery(id+"F0.wireOp",EDGE,"E9.5.2"),sQuery(id+"F0.wireOp",EDGE,"E9.5.3"),sQuery(id+"F0.wireOp",EDGE,"E9.5.4"),sQuery(id+"F0.wireOp",EDGE,"E9.5.5"),sQuery(id+"F0.wireOp",EDGE,"E9.5.6"),sQuery(id+"F0.wireOp",EDGE,"E9.5.7"),sQuery(id+"F0.wireOp",EDGE,"E9.5.8"),sQuery(id+"F0.wireOp",EDGE,"E10.0"),sQuery(id+"F0.wireOp",EDGE,"E10.1"),sQuery(id+"F0.wireOp",EDGE,"E10.2"),subQ5,sQuery(id+"F0.wireOp",EDGE,"E10.4"),sQuery(id+"F0.wireOp",EDGE,"E10.5"),subQ1,sQuery(id+"F0.wireOp",EDGE,"E15.trimOffspring"),sQuery(id+"F0.wireOp",EDGE,"E17.trimOffspring"),sQuery(id+"F0.wireOp",EDGE,"E21.trimOffspring"),sQuery(id+"F0.wireOp",EDGE,"E24.trimOffspring"),sQuery(id+"F0.wireOp",EDGE,"E27.trimOffspring")])],"isStart":false})});}
            var sketch = newSketch(context, id + "F15", { "sketchPlane" : qUnion([Q0])});
            skLineSegment(sketch, "E42", {"start": v(0, 0) * mm, "end": v(0, 50) * mm, "construction": true});
            skText(sketch, "E43", { "text": "Z", "fontName": "OpenSans-Regular.ttf"});
            skPoint(sketch, "E44", {"position": v(0, 50) * mm});
            skLineSegment(sketch, "E45.1.0", {"start": v(0, 0) * mm, "end": v(-43.3, -25) * mm, "construction": true});
            skLineSegment(sketch, "E45.2.0", {"start": v(0, 0) * mm, "end": v(43.3, -25) * mm, "construction": true});
            skPoint(sketch, "E45.center", {"position": v(0, 0) * mm});
            skText(sketch, "E46", { "text": "X", "fontName": "OpenSans-Regular.ttf"});
            skText(sketch, "E47", { "text": "Y", "fontName": "OpenSans-Regular.ttf"});
            skPoint(sketch, "E48", {"position": v(-43.3, -25) * mm});
            skPoint(sketch, "E49", {"position": v(43.3, -25) * mm});
            const initialGuessF15  = {"E43": [-0.0029, 0.0465, 1, 0, 0.007], "E46": [-0.0464, -0.0285, 1, 0, 0.007], "E47": [0.04026, -0.0285, 1, 0, 0.007]};
            skSetInitialGuess(sketch, initialGuessF15);
            skSolve(sketch);
        }
        {
            var Q0;
            Q0 = qSketchRegion(id + "F14", true);
            var Q1;
            Q1 = qSketchRegion(id + "F15", true);
            extrude(context, id + "F16", {"entities" : qUnion([Q0, Q1]), "operationType" : NewBodyOperationType.REMOVE, "oppositeDirection" : true, "depth" : 0.5 * mm, "offsetDistance" : 25 * mm});
        }
        {
            var Q0;
            {var subQ0=sQuery(id+"F0.wireOp",EDGE,"E27.trimOffspring");var subQ1=sQuery(id+"F0.wireOp",EDGE,"E24.trimOffspring");var subQ2=sQuery(id+"F0.wireOp",EDGE,"E21.trimOffspring");var subQ3=sQuery(id+"F0.wireOp",EDGE,"E17.trimOffspring");var subQ4=sQuery(id+"F0.wireOp",EDGE,"E15.trimOffspring");var subQ5=sQuery(id+"F0.wireOp",EDGE,"E11.trimOffspring");var subQ6=sQuery(id+"F0.wireOp",EDGE,"E10.5");var subQ7=sQuery(id+"F0.wireOp",EDGE,"E10.4");var subQ8=sQuery(id+"F0.wireOp",EDGE,"E10.3");var subQ9=sQuery(id+"F0.wireOp",EDGE,"E10.2");var subQ10=sQuery(id+"F0.wireOp",EDGE,"E10.1");var subQ11=sQuery(id+"F0.wireOp",EDGE,"E10.0");var subQ12=sQuery(id+"F0.wireOp",EDGE,"E9.5.8");var subQ13=sQuery(id+"F0.wireOp",EDGE,"E9.5.7");var subQ14=sQuery(id+"F0.wireOp",EDGE,"E9.5.6");var subQ15=sQuery(id+"F0.wireOp",EDGE,"E9.5.5");var subQ16=sQuery(id+"F0.wireOp",EDGE,"E9.5.4");var subQ17=sQuery(id+"F0.wireOp",EDGE,"E9.5.3");var subQ18=sQuery(id+"F0.wireOp",EDGE,"E9.3.5");var subQ19=sQuery(id+"F0.wireOp",EDGE,"E9.2.5");var subQ20=sQuery(id+"F0.wireOp",EDGE,"E9.3.4");var subQ21=sQuery(id+"F0.wireOp",EDGE,"E9.2.4");var subQ22=sQuery(id+"F0.wireOp",EDGE,"E9.3.3");var subQ23=sQuery(id+"F0.wireOp",EDGE,"E9.2.3");var subQ24=sQuery(id+"F0.wireOp",EDGE,"E9.3.2");var subQ25=sQuery(id+"F0.wireOp",EDGE,"E9.2.2");var subQ26=sQuery(id+"F0.wireOp",EDGE,"E9.3.1");var subQ27=sQuery(id+"F0.wireOp",EDGE,"E9.2.1");var subQ28=sQuery(id+"F0.wireOp",EDGE,"E9.2.0");var subQ29=sQuery(id+"F0.wireOp",EDGE,"E9.1.8");var subQ30=sQuery(id+"F0.wireOp",EDGE,"E9.2.7");var subQ31=sQuery(id+"F0.wireOp",EDGE,"E9.1.7");var subQ32=sQuery(id+"F0.wireOp",EDGE,"E9.1.6");var subQ33=sQuery(id+"F0.wireOp",EDGE,"E9.1.5");var subQ34=sQuery(id+"F0.wireOp",EDGE,"E9.1.4");var subQ35=sQuery(id+"F0.wireOp",EDGE,"E9.1.3");var subQ36=sQuery(id+"F0.wireOp",EDGE,"E7.3");var subQ37=sQuery(id+"F0.wireOp",EDGE,"E7.2");var subQ38=sQuery(id+"F0.wireOp",EDGE,"E7.1");var subQ39=sQuery(id+"F0.wireOp",EDGE,"E7.0");var subQ40=sQuery(id+"F0.wireOp",EDGE,"E7.4");var subQ41=sQuery(id+"F0.wireOp",EDGE,"E7.5");var subQ42=sQuery(id+"F0.wireOp",EDGE,"E8.trimOffspring");var subQ43=sQuery(id+"F0.wireOp",EDGE,"E9.1.0");var subQ44=sQuery(id+"F0.wireOp",EDGE,"E9.1.1");var subQ45=sQuery(id+"F0.wireOp",EDGE,"E9.1.2");var subQ46=sQuery(id+"F0.wireOp",EDGE,"E9.3.6");var subQ47=sQuery(id+"F0.wireOp",EDGE,"E9.2.6");var subQ48=sQuery(id+"F0.wireOp",EDGE,"E9.2.8");var subQ49=sQuery(id+"F0.wireOp",EDGE,"E9.4.0");var subQ50=sQuery(id+"F0.wireOp",EDGE,"E9.3.0");var subQ51=sQuery(id+"F0.wireOp",EDGE,"E9.4.1");var subQ52=sQuery(id+"F0.wireOp",EDGE,"E9.4.2");var subQ53=sQuery(id+"F0.wireOp",EDGE,"E9.4.3");var subQ54=sQuery(id+"F0.wireOp",EDGE,"E9.4.4");var subQ55=sQuery(id+"F0.wireOp",EDGE,"E9.4.5");var subQ56=sQuery(id+"F0.wireOp",EDGE,"E9.3.7");var subQ57=sQuery(id+"F0.wireOp",EDGE,"E9.4.8");var subQ58=sQuery(id+"F0.wireOp",EDGE,"E5.right");var subQ59=sQuery(id+"F0.wireOp",EDGE,"E9.3.8");var subQ60=sQuery(id+"F0.wireOp",EDGE,"E9.5.0");var subQ61=sQuery(id+"F0.wireOp",EDGE,"E9.5.1");var subQ62=sQuery(id+"F0.wireOp",EDGE,"E9.5.2");var subQ63=sQuery(id+"F0.wireOp",EDGE,"E9.4.6");var subQ64=sQuery(id+"F0.wireOp",EDGE,"E9.4.7");var subQ65=sQuery(id+"F0.wireOp",EDGE,"E5.left");Q0=makeQuery(id+"F10.boolean.opBoolean","SPLIT",FACE,{"disambiguationData":[TD([makeQuery(id+"F1.opExtrude","SWEPT_FACE",FACE,{"disambiguationData":[OSD([subQ39])]})])],"derivedFrom":makeQuery(id+"F1.opExtrude","CAP_FACE",FACE,{"disambiguationData":[OSD([subQ65,subQ58,subQ39,subQ38,subQ37,subQ36,subQ40,subQ41,subQ42,subQ43,subQ44,subQ45,subQ35,subQ34,subQ33,subQ32,subQ31,subQ29,subQ28,subQ27,subQ25,subQ23,subQ21,subQ19,subQ47,subQ30,subQ48,subQ50,subQ26,subQ24,subQ22,subQ20,subQ18,subQ46,subQ56,subQ59,subQ49,subQ51,subQ52,subQ53,subQ54,subQ55,subQ63,subQ64,subQ57,subQ60,subQ61,subQ62,subQ17,subQ16,subQ15,subQ14,subQ13,subQ12,subQ11,subQ10,subQ9,subQ8,subQ7,subQ6,subQ5,subQ4,subQ3,subQ2,subQ1,subQ0])],"isStart":true})});}
            var sketch = newSketch(context, id + "F17", { "sketchPlane" : qUnion([Q0])});
            skCircle(sketch, "E50", {"center": v(0, -82.5) * mm, "radius": 9 * mm});
            skCircle(sketch, "E51", {"center": v(0, -82.5) * mm, "radius": 4 * mm});
            skCircle(sketch, "E52.1.0", {"center": v(71.45, -41.25) * mm, "radius": 9 * mm});
            skCircle(sketch, "E52.1.1", {"center": v(71.45, -41.25) * mm, "radius": 4 * mm});
            skCircle(sketch, "E52.2.0", {"center": v(71.45, 41.25) * mm, "radius": 9 * mm});
            skCircle(sketch, "E52.2.1", {"center": v(71.45, 41.25) * mm, "radius": 4 * mm});
            skCircle(sketch, "E52.3.0", {"center": v(0, 82.5) * mm, "radius": 9 * mm});
            skCircle(sketch, "E52.3.1", {"center": v(0, 82.5) * mm, "radius": 4 * mm});
            skCircle(sketch, "E52.4.0", {"center": v(-71.45, 41.25) * mm, "radius": 9 * mm});
            skCircle(sketch, "E52.4.1", {"center": v(-71.45, 41.25) * mm, "radius": 4 * mm});
            skCircle(sketch, "E52.5.0", {"center": v(-71.45, -41.25) * mm, "radius": 9 * mm});
            skCircle(sketch, "E52.5.1", {"center": v(-71.45, -41.25) * mm, "radius": 4 * mm});
            skPoint(sketch, "E52.center", {"position": v(0, 0) * mm});
            skSolve(sketch);
        }
        {
            var Q0;
            Q0 = qSketchRegion(id + "F17", true);
            extrude(context, id + "F18", {"entities" : qUnion([Q0]), "operationType" : NewBodyOperationType.REMOVE, "oppositeDirection" : true, "depth" : 0.5 * mm, "offsetDistance" : 25 * mm});
        }
        {
            var Q0;
            Q0=makeQuery(id+"F1.opExtrude","CAP_EDGE",EDGE,{"disambiguationData":[OSD([sQuery(id+"F0.wireOp",EDGE,"E9.3.4")])],"isStart":true});
            var Q1;
            Q1=makeQuery(id+"F1.opExtrude","CAP_EDGE",EDGE,{"disambiguationData":[OSD([sQuery(id+"F0.wireOp",EDGE,"E9.4.2")])],"isStart":true});
            var Q2;
            Q2=makeQuery(id+"F1.opExtrude","CAP_EDGE",EDGE,{"disambiguationData":[OSD([sQuery(id+"F0.wireOp",EDGE,"E9.2.4")])],"isStart":true});
            var Q3;
            Q3=makeQuery(id+"F1.opExtrude","CAP_EDGE",EDGE,{"disambiguationData":[OSD([sQuery(id+"F0.wireOp",EDGE,"E9.1.4")])],"isStart":true});
            var Q4;
            Q4=makeQuery(id+"F1.opExtrude","CAP_EDGE",EDGE,{"disambiguationData":[OSD([sQuery(id+"F0.wireOp",EDGE,"E7.1")])],"isStart":true});
            var Q5;
            Q5=makeQuery(id+"F1.opExtrude","CAP_EDGE",EDGE,{"disambiguationData":[OSD([sQuery(id+"F0.wireOp",EDGE,"E9.5.2")])],"isStart":true});
            var Q6;
            Q6=makeQuery(id+"F1.opExtrude","CAP_EDGE",EDGE,{"disambiguationData":[OSD([sQuery(id+"F0.wireOp",EDGE,"E10.5")])],"isStart":true});
            var Q7;
            Q7=makeQuery(id+"F1.opExtrude","CAP_EDGE",EDGE,{"disambiguationData":[OSD([sQuery(id+"F0.wireOp",EDGE,"E11.trimOffspring")])],"isStart":true});
            var Q8;
            Q8=makeQuery(id+"F1.opExtrude","CAP_EDGE",EDGE,{"disambiguationData":[OSD([sQuery(id+"F0.wireOp",EDGE,"E10.3")])],"isStart":true});
            var Q9;
            Q9=makeQuery(id+"F1.opExtrude","CAP_EDGE",EDGE,{"disambiguationData":[OSD([sQuery(id+"F0.wireOp",EDGE,"E10.2")])],"isStart":true});
            var Q10;
            Q10=makeQuery(id+"F1.opExtrude","CAP_EDGE",EDGE,{"disambiguationData":[OSD([sQuery(id+"F0.wireOp",EDGE,"E10.0")])],"isStart":true});
            var Q11;
            Q11=makeQuery(id+"F1.opExtrude","CAP_EDGE",EDGE,{"disambiguationData":[OSD([sQuery(id+"F0.wireOp",EDGE,"E9.4.8")])],"isStart":true});
            var Q12;
            Q12=makeQuery(id+"F1.opExtrude","CAP_EDGE",EDGE,{"disambiguationData":[OSD([sQuery(id+"F0.wireOp",EDGE,"E9.4.7")])],"isStart":true});
            var Q13;
            Q13=makeQuery(id+"F1.opExtrude","CAP_EDGE",EDGE,{"disambiguationData":[OSD([sQuery(id+"F0.wireOp",EDGE,"E9.5.8")])],"isStart":true});
            var Q14;
            Q14=makeQuery(id+"F1.opExtrude","CAP_EDGE",EDGE,{"disambiguationData":[OSD([sQuery(id+"F0.wireOp",EDGE,"E9.5.7")])],"isStart":true});
            var Q15;
            {var subQ0=sQuery(id+"F0.wireOp",EDGE,"E5.right");Q15=makeQuery(id+"F4.opChamfer","BLEND_EDGE",EDGE,{"blendedFrom":[makeQuery(id+"F1.opExtrude","CAP_EDGE",EDGE,{"disambiguationData":[OSD([subQ0])],"isStart":true}),makeQuery(id+"F1.opExtrude","CAP_FACE",FACE,{"disambiguationData":[OSD([sQuery(id+"F0.wireOp",EDGE,"E5.left"),subQ0,sQuery(id+"F0.wireOp",EDGE,"E7.0"),sQuery(id+"F0.wireOp",EDGE,"E7.1"),sQuery(id+"F0.wireOp",EDGE,"E7.2"),sQuery(id+"F0.wireOp",EDGE,"E7.3"),sQuery(id+"F0.wireOp",EDGE,"E7.4"),sQuery(id+"F0.wireOp",EDGE,"E7.5"),sQuery(id+"F0.wireOp",EDGE,"E8.trimOffspring"),sQuery(id+"F0.wireOp",EDGE,"E9.1.0"),sQuery(id+"F0.wireOp",EDGE,"E9.1.1"),sQuery(id+"F0.wireOp",EDGE,"E9.1.2"),sQuery(id+"F0.wireOp",EDGE,"E9.1.3"),sQuery(id+"F0.wireOp",EDGE,"E9.1.4"),sQuery(id+"F0.wireOp",EDGE,"E9.1.5"),sQuery(id+"F0.wireOp",EDGE,"E9.1.6"),sQuery(id+"F0.wireOp",EDGE,"E9.1.7"),sQuery(id+"F0.wireOp",EDGE,"E9.1.8"),sQuery(id+"F0.wireOp",EDGE,"E9.2.0"),sQuery(id+"F0.wireOp",EDGE,"E9.2.1"),sQuery(id+"F0.wireOp",EDGE,"E9.2.2"),sQuery(id+"F0.wireOp",EDGE,"E9.2.3"),sQuery(id+"F0.wireOp",EDGE,"E9.2.4"),sQuery(id+"F0.wireOp",EDGE,"E9.2.5"),sQuery(id+"F0.wireOp",EDGE,"E9.2.6"),sQuery(id+"F0.wireOp",EDGE,"E9.2.7"),sQuery(id+"F0.wireOp",EDGE,"E9.2.8"),sQuery(id+"F0.wireOp",EDGE,"E9.3.0"),sQuery(id+"F0.wireOp",EDGE,"E9.3.1"),sQuery(id+"F0.wireOp",EDGE,"E9.3.2"),sQuery(id+"F0.wireOp",EDGE,"E9.3.3"),sQuery(id+"F0.wireOp",EDGE,"E9.3.4"),sQuery(id+"F0.wireOp",EDGE,"E9.3.5"),sQuery(id+"F0.wireOp",EDGE,"E9.3.6"),sQuery(id+"F0.wireOp",EDGE,"E9.3.7"),sQuery(id+"F0.wireOp",EDGE,"E9.3.8"),sQuery(id+"F0.wireOp",EDGE,"E9.4.0"),sQuery(id+"F0.wireOp",EDGE,"E9.4.1"),sQuery(id+"F0.wireOp",EDGE,"E9.4.2"),sQuery(id+"F0.wireOp",EDGE,"E9.4.3"),sQuery(id+"F0.wireOp",EDGE,"E9.4.4"),sQuery(id+"F0.wireOp",EDGE,"E9.4.5"),sQuery(id+"F0.wireOp",EDGE,"E9.4.6"),sQuery(id+"F0.wireOp",EDGE,"E9.4.7"),sQuery(id+"F0.wireOp",EDGE,"E9.4.8"),sQuery(id+"F0.wireOp",EDGE,"E9.5.0"),sQuery(id+"F0.wireOp",EDGE,"E9.5.1"),sQuery(id+"F0.wireOp",EDGE,"E9.5.2"),sQuery(id+"F0.wireOp",EDGE,"E9.5.3"),sQuery(id+"F0.wireOp",EDGE,"E9.5.4"),sQuery(id+"F0.wireOp",EDGE,"E9.5.5"),sQuery(id+"F0.wireOp",EDGE,"E9.5.6"),sQuery(id+"F0.wireOp",EDGE,"E9.5.7"),sQuery(id+"F0.wireOp",EDGE,"E9.5.8"),sQuery(id+"F0.wireOp",EDGE,"E10.0"),sQuery(id+"F0.wireOp",EDGE,"E10.1"),sQuery(id+"F0.wireOp",EDGE,"E10.2"),sQuery(id+"F0.wireOp",EDGE,"E10.3"),sQuery(id+"F0.wireOp",EDGE,"E10.4"),sQuery(id+"F0.wireOp",EDGE,"E10.5"),sQuery(id+"F0.wireOp",EDGE,"E11.trimOffspring"),sQuery(id+"F0.wireOp",EDGE,"E15.trimOffspring"),sQuery(id+"F0.wireOp",EDGE,"E17.trimOffspring"),sQuery(id+"F0.wireOp",EDGE,"E21.trimOffspring"),sQuery(id+"F0.wireOp",EDGE,"E24.trimOffspring"),sQuery(id+"F0.wireOp",EDGE,"E27.trimOffspring")])],"isStart":true})],"blendedInto":[makeQuery(id+"F1.opExtrude","CAP_FACE",FACE,{"disambiguationData":[OSD([sQuery(id+"F0.wireOp",EDGE,"E5.left"),subQ0,sQuery(id+"F0.wireOp",EDGE,"E7.0"),sQuery(id+"F0.wireOp",EDGE,"E7.1"),sQuery(id+"F0.wireOp",EDGE,"E7.2"),sQuery(id+"F0.wireOp",EDGE,"E7.3"),sQuery(id+"F0.wireOp",EDGE,"E7.4"),sQuery(id+"F0.wireOp",EDGE,"E7.5"),sQuery(id+"F0.wireOp",EDGE,"E8.trimOffspring"),sQuery(id+"F0.wireOp",EDGE,"E9.1.0"),sQuery(id+"F0.wireOp",EDGE,"E9.1.1"),sQuery(id+"F0.wireOp",EDGE,"E9.1.2"),sQuery(id+"F0.wireOp",EDGE,"E9.1.3"),sQuery(id+"F0.wireOp",EDGE,"E9.1.4"),sQuery(id+"F0.wireOp",EDGE,"E9.1.5"),sQuery(id+"F0.wireOp",EDGE,"E9.1.6"),sQuery(id+"F0.wireOp",EDGE,"E9.1.7"),sQuery(id+"F0.wireOp",EDGE,"E9.1.8"),sQuery(id+"F0.wireOp",EDGE,"E9.2.0"),sQuery(id+"F0.wireOp",EDGE,"E9.2.1"),sQuery(id+"F0.wireOp",EDGE,"E9.2.2"),sQuery(id+"F0.wireOp",EDGE,"E9.2.3"),sQuery(id+"F0.wireOp",EDGE,"E9.2.4"),sQuery(id+"F0.wireOp",EDGE,"E9.2.5"),sQuery(id+"F0.wireOp",EDGE,"E9.2.6"),sQuery(id+"F0.wireOp",EDGE,"E9.2.7"),sQuery(id+"F0.wireOp",EDGE,"E9.2.8"),sQuery(id+"F0.wireOp",EDGE,"E9.3.0"),sQuery(id+"F0.wireOp",EDGE,"E9.3.1"),sQuery(id+"F0.wireOp",EDGE,"E9.3.2"),sQuery(id+"F0.wireOp",EDGE,"E9.3.3"),sQuery(id+"F0.wireOp",EDGE,"E9.3.4"),sQuery(id+"F0.wireOp",EDGE,"E9.3.5"),sQuery(id+"F0.wireOp",EDGE,"E9.3.6"),sQuery(id+"F0.wireOp",EDGE,"E9.3.7"),sQuery(id+"F0.wireOp",EDGE,"E9.3.8"),sQuery(id+"F0.wireOp",EDGE,"E9.4.0"),sQuery(id+"F0.wireOp",EDGE,"E9.4.1"),sQuery(id+"F0.wireOp",EDGE,"E9.4.2"),sQuery(id+"F0.wireOp",EDGE,"E9.4.3"),sQuery(id+"F0.wireOp",EDGE,"E9.4.4"),sQuery(id+"F0.wireOp",EDGE,"E9.4.5"),sQuery(id+"F0.wireOp",EDGE,"E9.4.6"),sQuery(id+"F0.wireOp",EDGE,"E9.4.7"),sQuery(id+"F0.wireOp",EDGE,"E9.4.8"),sQuery(id+"F0.wireOp",EDGE,"E9.5.0"),sQuery(id+"F0.wireOp",EDGE,"E9.5.1"),sQuery(id+"F0.wireOp",EDGE,"E9.5.2"),sQuery(id+"F0.wireOp",EDGE,"E9.5.3"),sQuery(id+"F0.wireOp",EDGE,"E9.5.4"),sQuery(id+"F0.wireOp",EDGE,"E9.5.5"),sQuery(id+"F0.wireOp",EDGE,"E9.5.6"),sQuery(id+"F0.wireOp",EDGE,"E9.5.7"),sQuery(id+"F0.wireOp",EDGE,"E9.5.8"),sQuery(id+"F0.wireOp",EDGE,"E10.0"),sQuery(id+"F0.wireOp",EDGE,"E10.1"),sQuery(id+"F0.wireOp",EDGE,"E10.2"),sQuery(id+"F0.wireOp",EDGE,"E10.3"),sQuery(id+"F0.wireOp",EDGE,"E10.4"),sQuery(id+"F0.wireOp",EDGE,"E10.5"),sQuery(id+"F0.wireOp",EDGE,"E11.trimOffspring"),sQuery(id+"F0.wireOp",EDGE,"E15.trimOffspring"),sQuery(id+"F0.wireOp",EDGE,"E17.trimOffspring"),sQuery(id+"F0.wireOp",EDGE,"E21.trimOffspring"),sQuery(id+"F0.wireOp",EDGE,"E24.trimOffspring"),sQuery(id+"F0.wireOp",EDGE,"E27.trimOffspring")])],"isStart":true})]});}
            var Q16;
            {var subQ0=sQuery(id+"F0.wireOp",EDGE,"E5.left");Q16=makeQuery(id+"F4.opChamfer","BLEND_EDGE",EDGE,{"blendedFrom":[makeQuery(id+"F1.opExtrude","CAP_EDGE",EDGE,{"disambiguationData":[OSD([subQ0])],"isStart":true}),makeQuery(id+"F1.opExtrude","CAP_FACE",FACE,{"disambiguationData":[OSD([subQ0,sQuery(id+"F0.wireOp",EDGE,"E5.right"),sQuery(id+"F0.wireOp",EDGE,"E7.0"),sQuery(id+"F0.wireOp",EDGE,"E7.1"),sQuery(id+"F0.wireOp",EDGE,"E7.2"),sQuery(id+"F0.wireOp",EDGE,"E7.3"),sQuery(id+"F0.wireOp",EDGE,"E7.4"),sQuery(id+"F0.wireOp",EDGE,"E7.5"),sQuery(id+"F0.wireOp",EDGE,"E8.trimOffspring"),sQuery(id+"F0.wireOp",EDGE,"E9.1.0"),sQuery(id+"F0.wireOp",EDGE,"E9.1.1"),sQuery(id+"F0.wireOp",EDGE,"E9.1.2"),sQuery(id+"F0.wireOp",EDGE,"E9.1.3"),sQuery(id+"F0.wireOp",EDGE,"E9.1.4"),sQuery(id+"F0.wireOp",EDGE,"E9.1.5"),sQuery(id+"F0.wireOp",EDGE,"E9.1.6"),sQuery(id+"F0.wireOp",EDGE,"E9.1.7"),sQuery(id+"F0.wireOp",EDGE,"E9.1.8"),sQuery(id+"F0.wireOp",EDGE,"E9.2.0"),sQuery(id+"F0.wireOp",EDGE,"E9.2.1"),sQuery(id+"F0.wireOp",EDGE,"E9.2.2"),sQuery(id+"F0.wireOp",EDGE,"E9.2.3"),sQuery(id+"F0.wireOp",EDGE,"E9.2.4"),sQuery(id+"F0.wireOp",EDGE,"E9.2.5"),sQuery(id+"F0.wireOp",EDGE,"E9.2.6"),sQuery(id+"F0.wireOp",EDGE,"E9.2.7"),sQuery(id+"F0.wireOp",EDGE,"E9.2.8"),sQuery(id+"F0.wireOp",EDGE,"E9.3.0"),sQuery(id+"F0.wireOp",EDGE,"E9.3.1"),sQuery(id+"F0.wireOp",EDGE,"E9.3.2"),sQuery(id+"F0.wireOp",EDGE,"E9.3.3"),sQuery(id+"F0.wireOp",EDGE,"E9.3.4"),sQuery(id+"F0.wireOp",EDGE,"E9.3.5"),sQuery(id+"F0.wireOp",EDGE,"E9.3.6"),sQuery(id+"F0.wireOp",EDGE,"E9.3.7"),sQuery(id+"F0.wireOp",EDGE,"E9.3.8"),sQuery(id+"F0.wireOp",EDGE,"E9.4.0"),sQuery(id+"F0.wireOp",EDGE,"E9.4.1"),sQuery(id+"F0.wireOp",EDGE,"E9.4.2"),sQuery(id+"F0.wireOp",EDGE,"E9.4.3"),sQuery(id+"F0.wireOp",EDGE,"E9.4.4"),sQuery(id+"F0.wireOp",EDGE,"E9.4.5"),sQuery(id+"F0.wireOp",EDGE,"E9.4.6"),sQuery(id+"F0.wireOp",EDGE,"E9.4.7"),sQuery(id+"F0.wireOp",EDGE,"E9.4.8"),sQuery(id+"F0.wireOp",EDGE,"E9.5.0"),sQuery(id+"F0.wireOp",EDGE,"E9.5.1"),sQuery(id+"F0.wireOp",EDGE,"E9.5.2"),sQuery(id+"F0.wireOp",EDGE,"E9.5.3"),sQuery(id+"F0.wireOp",EDGE,"E9.5.4"),sQuery(id+"F0.wireOp",EDGE,"E9.5.5"),sQuery(id+"F0.wireOp",EDGE,"E9.5.6"),sQuery(id+"F0.wireOp",EDGE,"E9.5.7"),sQuery(id+"F0.wireOp",EDGE,"E9.5.8"),sQuery(id+"F0.wireOp",EDGE,"E10.0"),sQuery(id+"F0.wireOp",EDGE,"E10.1"),sQuery(id+"F0.wireOp",EDGE,"E10.2"),sQuery(id+"F0.wireOp",EDGE,"E10.3"),sQuery(id+"F0.wireOp",EDGE,"E10.4"),sQuery(id+"F0.wireOp",EDGE,"E10.5"),sQuery(id+"F0.wireOp",EDGE,"E11.trimOffspring"),sQuery(id+"F0.wireOp",EDGE,"E15.trimOffspring"),sQuery(id+"F0.wireOp",EDGE,"E17.trimOffspring"),sQuery(id+"F0.wireOp",EDGE,"E21.trimOffspring"),sQuery(id+"F0.wireOp",EDGE,"E24.trimOffspring"),sQuery(id+"F0.wireOp",EDGE,"E27.trimOffspring")])],"isStart":true})],"blendedInto":[makeQuery(id+"F1.opExtrude","CAP_FACE",FACE,{"disambiguationData":[OSD([subQ0,sQuery(id+"F0.wireOp",EDGE,"E5.right"),sQuery(id+"F0.wireOp",EDGE,"E7.0"),sQuery(id+"F0.wireOp",EDGE,"E7.1"),sQuery(id+"F0.wireOp",EDGE,"E7.2"),sQuery(id+"F0.wireOp",EDGE,"E7.3"),sQuery(id+"F0.wireOp",EDGE,"E7.4"),sQuery(id+"F0.wireOp",EDGE,"E7.5"),sQuery(id+"F0.wireOp",EDGE,"E8.trimOffspring"),sQuery(id+"F0.wireOp",EDGE,"E9.1.0"),sQuery(id+"F0.wireOp",EDGE,"E9.1.1"),sQuery(id+"F0.wireOp",EDGE,"E9.1.2"),sQuery(id+"F0.wireOp",EDGE,"E9.1.3"),sQuery(id+"F0.wireOp",EDGE,"E9.1.4"),sQuery(id+"F0.wireOp",EDGE,"E9.1.5"),sQuery(id+"F0.wireOp",EDGE,"E9.1.6"),sQuery(id+"F0.wireOp",EDGE,"E9.1.7"),sQuery(id+"F0.wireOp",EDGE,"E9.1.8"),sQuery(id+"F0.wireOp",EDGE,"E9.2.0"),sQuery(id+"F0.wireOp",EDGE,"E9.2.1"),sQuery(id+"F0.wireOp",EDGE,"E9.2.2"),sQuery(id+"F0.wireOp",EDGE,"E9.2.3"),sQuery(id+"F0.wireOp",EDGE,"E9.2.4"),sQuery(id+"F0.wireOp",EDGE,"E9.2.5"),sQuery(id+"F0.wireOp",EDGE,"E9.2.6"),sQuery(id+"F0.wireOp",EDGE,"E9.2.7"),sQuery(id+"F0.wireOp",EDGE,"E9.2.8"),sQuery(id+"F0.wireOp",EDGE,"E9.3.0"),sQuery(id+"F0.wireOp",EDGE,"E9.3.1"),sQuery(id+"F0.wireOp",EDGE,"E9.3.2"),sQuery(id+"F0.wireOp",EDGE,"E9.3.3"),sQuery(id+"F0.wireOp",EDGE,"E9.3.4"),sQuery(id+"F0.wireOp",EDGE,"E9.3.5"),sQuery(id+"F0.wireOp",EDGE,"E9.3.6"),sQuery(id+"F0.wireOp",EDGE,"E9.3.7"),sQuery(id+"F0.wireOp",EDGE,"E9.3.8"),sQuery(id+"F0.wireOp",EDGE,"E9.4.0"),sQuery(id+"F0.wireOp",EDGE,"E9.4.1"),sQuery(id+"F0.wireOp",EDGE,"E9.4.2"),sQuery(id+"F0.wireOp",EDGE,"E9.4.3"),sQuery(id+"F0.wireOp",EDGE,"E9.4.4"),sQuery(id+"F0.wireOp",EDGE,"E9.4.5"),sQuery(id+"F0.wireOp",EDGE,"E9.4.6"),sQuery(id+"F0.wireOp",EDGE,"E9.4.7"),sQuery(id+"F0.wireOp",EDGE,"E9.4.8"),sQuery(id+"F0.wireOp",EDGE,"E9.5.0"),sQuery(id+"F0.wireOp",EDGE,"E9.5.1"),sQuery(id+"F0.wireOp",EDGE,"E9.5.2"),sQuery(id+"F0.wireOp",EDGE,"E9.5.3"),sQuery(id+"F0.wireOp",EDGE,"E9.5.4"),sQuery(id+"F0.wireOp",EDGE,"E9.5.5"),sQuery(id+"F0.wireOp",EDGE,"E9.5.6"),sQuery(id+"F0.wireOp",EDGE,"E9.5.7"),sQuery(id+"F0.wireOp",EDGE,"E9.5.8"),sQuery(id+"F0.wireOp",EDGE,"E10.0"),sQuery(id+"F0.wireOp",EDGE,"E10.1"),sQuery(id+"F0.wireOp",EDGE,"E10.2"),sQuery(id+"F0.wireOp",EDGE,"E10.3"),sQuery(id+"F0.wireOp",EDGE,"E10.4"),sQuery(id+"F0.wireOp",EDGE,"E10.5"),sQuery(id+"F0.wireOp",EDGE,"E11.trimOffspring"),sQuery(id+"F0.wireOp",EDGE,"E15.trimOffspring"),sQuery(id+"F0.wireOp",EDGE,"E17.trimOffspring"),sQuery(id+"F0.wireOp",EDGE,"E21.trimOffspring"),sQuery(id+"F0.wireOp",EDGE,"E24.trimOffspring"),sQuery(id+"F0.wireOp",EDGE,"E27.trimOffspring")])],"isStart":true})]});}
            var Q17;
            Q17=makeQuery(id+"F1.opExtrude","CAP_EDGE",EDGE,{"disambiguationData":[OSD([sQuery(id+"F0.wireOp",EDGE,"E9.3.7")])],"isStart":true});
            var Q18;
            Q18=makeQuery(id+"F1.opExtrude","CAP_EDGE",EDGE,{"disambiguationData":[OSD([sQuery(id+"F0.wireOp",EDGE,"E9.3.8")])],"isStart":true});
            var Q19;
            Q19=makeQuery(id+"F1.opExtrude","CAP_EDGE",EDGE,{"disambiguationData":[OSD([sQuery(id+"F0.wireOp",EDGE,"E9.2.7")])],"isStart":true});
            var Q20;
            Q20=makeQuery(id+"F1.opExtrude","CAP_EDGE",EDGE,{"disambiguationData":[OSD([sQuery(id+"F0.wireOp",EDGE,"E9.2.8")])],"isStart":true});
            var Q21;
            Q21=makeQuery(id+"F1.opExtrude","CAP_EDGE",EDGE,{"disambiguationData":[OSD([sQuery(id+"F0.wireOp",EDGE,"E9.1.7")])],"isStart":true});
            var Q22;
            Q22=makeQuery(id+"F1.opExtrude","CAP_EDGE",EDGE,{"disambiguationData":[OSD([sQuery(id+"F0.wireOp",EDGE,"E9.1.8")])],"isStart":true});
            chamfer(context, id + "F19", {"entities" : qUnion([Q0, Q1, Q2, Q3, Q4, Q5, Q6, Q7, Q8, Q9, Q10, Q11, Q12, Q13, Q14, Q15, Q16, Q17, Q18, Q19, Q20, Q21, Q22]), "width" : 1 * mm, "tangentPropagation" : true});
        }
    });
